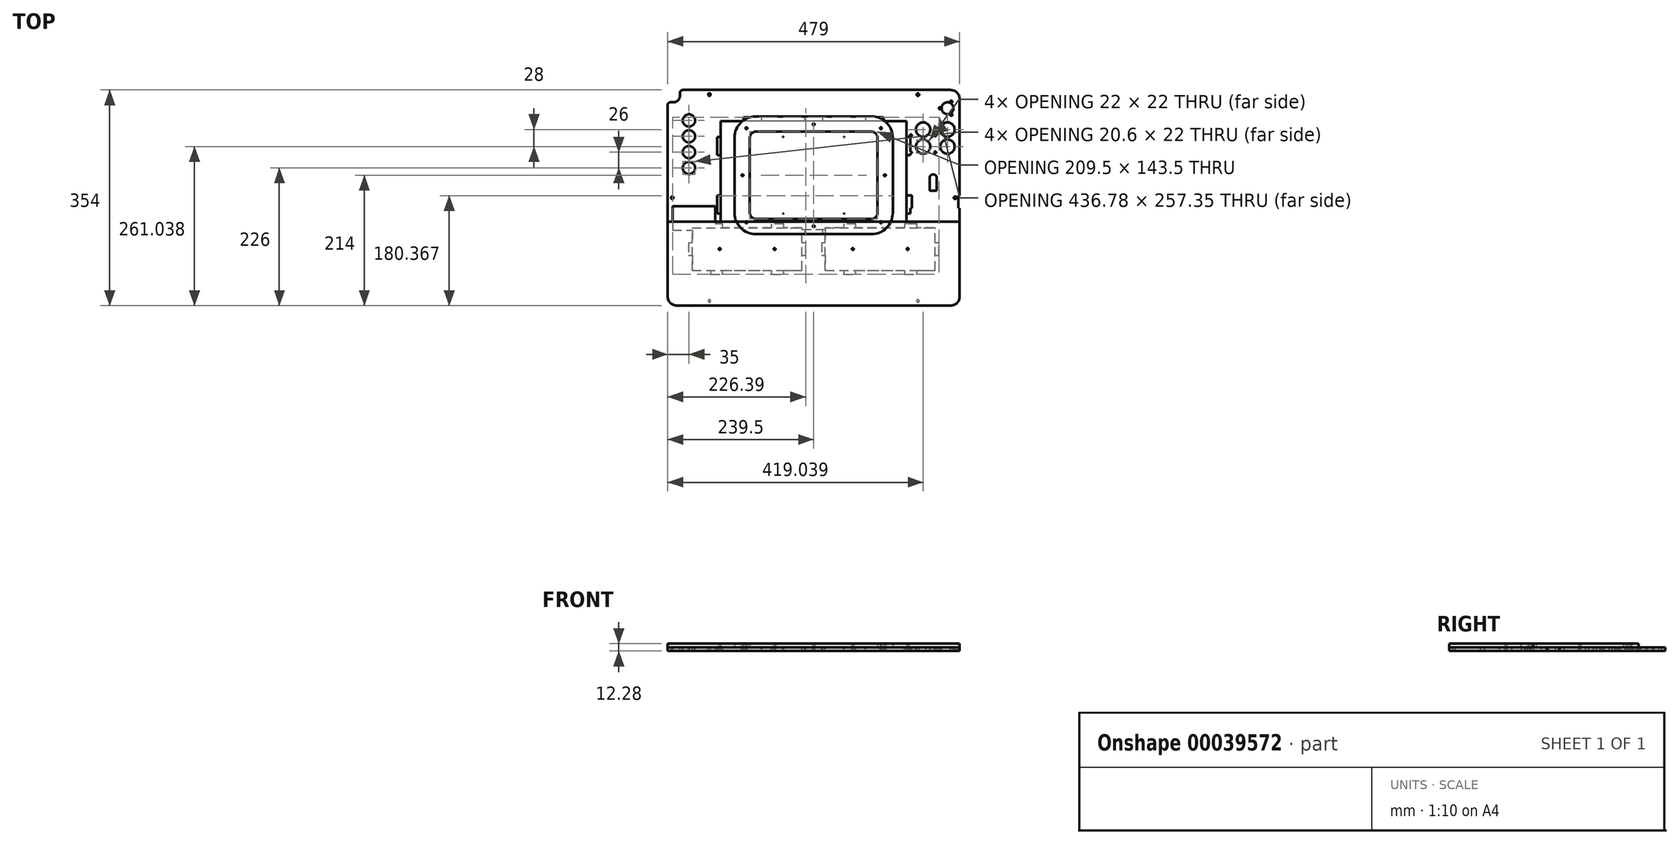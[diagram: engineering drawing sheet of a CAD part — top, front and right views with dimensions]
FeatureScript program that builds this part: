
annotation { "Feature Type Name" : "Feature", "Feature Type Description" : "" }
export const myFeature = defineFeature(function(context is Context, id is Id, definition is map)
    precondition{}
    {
        {
            assignVariable(context, id + "F0", {"name" : "PanelThickness", "anyValue" : 6.14});
        }
        {
            var Q0;
            Q0=qCreatedBy(makeId("Top.planeOp"),FACE);
            var sketch = newSketch(context, id + "F1", { "sketchPlane" : qUnion([Q0])});
            skPoint(sketch, "E0", {"position": v(168.5, 147.5) * mm});
            skPoint(sketch, "E1.visualSharp", {"position": v(237, -199) * mm});
            skPoint(sketch, "E2.visualSharp", {"position": v(-242, -199) * mm});
            skLineSegment(sketch, "E3.rect.right", {"start": v(237, 140) * mm, "end": v(237, -184) * mm});
            skPoint(sketch, "E4", {"position": v(229.5, -22) * mm});
            skPoint(sketch, "E5.visualSharp", {"position": v(-222, 135) * mm});
            skPoint(sketch, "E6.visualSharp", {"position": v(237, 155) * mm});
            skLineSegment(sketch, "E7", {"start": v(-249.24, -22) * mm, "end": v(312.3, -22) * mm, "construction": true});
            skPoint(sketch, "E8", {"position": v(-173.5, 147.5) * mm});
            skPoint(sketch, "E9.visualSharp", {"position": v(-242, 155) * mm});
            skLineSegment(sketch, "E10", {"start": v(0, 155) * mm, "end": v(0, -199) * mm, "construction": true});
            skLineSegment(sketch, "E11.0", {"start": v(-222, 147.5) * mm, "end": v(237, 147.5) * mm, "construction": true});
            skLineSegment(sketch, "E12.0", {"start": v(-242, -191.5) * mm, "end": v(237, -191.5) * mm, "construction": true});
            skLineSegment(sketch, "E13.0", {"start": v(-234.5, 155) * mm, "end": v(-234.5, -199) * mm, "construction": true});
            skLineSegment(sketch, "E3.rect.top", {"start": v(-227, -199) * mm, "end": v(222, -199) * mm});
            skLineSegment(sketch, "E3.rect.left", {"start": v(-242, 130) * mm, "end": v(-242, -184) * mm});
            skPoint(sketch, "E14", {"position": v(-234.5, -22) * mm});
            skLineSegment(sketch, "E3.rect.bottom", {"start": v(-217, 155) * mm, "end": v(222, 155) * mm});
            skLineSegment(sketch, "E15", {"start": v(168.5, -197.31) * mm, "end": v(168.5, 217.61) * mm, "construction": true});
            skLineSegment(sketch, "E16", {"start": v(-173.5, 155) * mm, "end": v(-173.5, -199) * mm, "construction": true});
            skLineSegment(sketch, "E17.0", {"start": v(229.5, 155) * mm, "end": v(229.5, -199) * mm, "construction": true});
            skLineSegment(sketch, "E18.left", {"start": v(-242, 146.2) * mm, "end": v(-242, 155) * mm, "construction": true});
            skLineSegment(sketch, "E18.bottom", {"start": v(-237, 135) * mm, "end": v(-232, 135) * mm});
            skCircle(sketch, "E19", {"center": v(-173.5, -191.5) * mm, "radius": 2.1 * mm});
            skArc(sketch, "E5.filletArc", {"start": v(-232, 135) * mm, "mid": v(-224.93, 137.93) * mm, "end": v(-222, 145) * mm});
            skCircle(sketch, "E20", {"center": v(168.5, 147.5) * mm, "radius": 2.1 * mm});
            skCircle(sketch, "E21", {"center": v(229.5, -22) * mm, "radius": 2.1 * mm});
            skCircle(sketch, "E22", {"center": v(168.5, -191.5) * mm, "radius": 2.1 * mm});
            skCircle(sketch, "E23", {"center": v(-234.5, -22) * mm, "radius": 2.1 * mm});
            skCircle(sketch, "E24", {"center": v(-173.5, 147.5) * mm, "radius": 2.1 * mm});
            skLineSegment(sketch, "E18.right", {"start": v(-222, 145) * mm, "end": v(-222, 150) * mm});
            skArc(sketch, "E25.filletArc", {"start": v(-237, 135) * mm, "mid": v(-240.54, 133.54) * mm, "end": v(-242, 130) * mm});
            skArc(sketch, "E26.filletArc", {"start": v(-217, 155) * mm, "mid": v(-220.54, 153.54) * mm, "end": v(-222, 150) * mm});
            skPoint(sketch, "E27", {"position": v(0, -22) * mm});
            skLineSegment(sketch, "E28", {"start": v(-242, 140) * mm, "end": v(-242, 130) * mm, "construction": true});
            skLineSegment(sketch, "E29", {"start": v(-234.5, 155) * mm, "end": v(-217, 155) * mm, "construction": true});
            skArc(sketch, "E30.filletArc", {"start": v(222, -199) * mm, "mid": v(232.6, -194.6) * mm, "end": v(237, -184) * mm});
            skArc(sketch, "E31.filletArc", {"start": v(-242, -184) * mm, "mid": v(-237.6, -194.6) * mm, "end": v(-227, -199) * mm});
            skArc(sketch, "E32.filletArc", {"start": v(237, 140) * mm, "mid": v(232.6, 150.6) * mm, "end": v(222, 155) * mm});
            skSolve(sketch);
        }
        {
            var Q0;
            Q0=qCreatedBy(makeId("Top.planeOp"),FACE);
            var sketch = newSketch(context, id + "F2", { "sketchPlane" : qUnion([Q0])});
            skLineSegment(sketch, "E33.bottom", {"start": v(-234, -36) * mm, "end": v(-164, -36) * mm});
            skLineSegment(sketch, "E33.top", {"start": v(-234, -75) * mm, "end": v(-164, -75) * mm});
            skLineSegment(sketch, "E33.right", {"start": v(-164, -36) * mm, "end": v(-164, -75) * mm});
            skLineSegment(sketch, "E33.left", {"start": v(-234, -36) * mm, "end": v(-234, -75) * mm});
            skLineSegment(sketch, "E34.0", {"start": v(-242, 130) * mm, "end": v(-242, -184) * mm});
            skLineSegment(sketch, "E35.0", {"start": v(-217, 155) * mm, "end": v(222, 155) * mm});
            skLineSegment(sketch, "E36.1", {"start": v(-238.1, -33.9) * mm, "end": v(-159.9, -33.9) * mm, "construction": true});
            skLineSegment(sketch, "E37.0", {"start": v(-159.9, -33.9) * mm, "end": v(-159.9, -77.1) * mm, "construction": true});
            skLineSegment(sketch, "E38.0", {"start": v(-238.1, -33.9) * mm, "end": v(-238.1, -77.1) * mm, "construction": true});
            skLineSegment(sketch, "E39.0", {"start": v(-238.1, -77.1) * mm, "end": v(-159.9, -77.1) * mm, "construction": true});
            skSolve(sketch);
        }
        {
            var Q0;
            Q0=qCreatedBy(makeId("Top.planeOp"),FACE);
            var sketch = newSketch(context, id + "F3", { "sketchPlane" : qUnion([Q0])});
            skLineSegment(sketch, "E40", {"start": v(-2.5, 81.1) * mm, "end": v(-2.5, -181.33) * mm, "construction": true});
            skLineSegment(sketch, "E41", {"start": v(-21.64, -116.17) * mm, "end": v(-21.64, -141.17) * mm});
            skLineSegment(sketch, "E42", {"start": v(-171.64, -71.17) * mm, "end": v(-201.64, -71.17) * mm});
            skLineSegment(sketch, "E43.0", {"start": v(-15.5, -65.03) * mm, "end": v(-15.5, -147.3) * mm, "construction": true});
            skLineSegment(sketch, "E44", {"start": v(-171.64, -141.17) * mm, "end": v(-201.64, -141.17) * mm});
            skLineSegment(sketch, "E45.MirrorCS", {"start": v(-71.64, -65.03) * mm, "end": v(-51.64, -65.03) * mm});
            skLineSegment(sketch, "E46.rect.bottom", {"start": v(-21.64, -71.17) * mm, "end": v(-51.64, -71.17) * mm});
            skLineSegment(sketch, "E46.rect.top", {"start": v(-21.64, -141.17) * mm, "end": v(-51.64, -141.17) * mm});
            skLineSegment(sketch, "E46.rect.left", {"start": v(-21.64, -71.17) * mm, "end": v(-21.64, -96.17) * mm});
            skLineSegment(sketch, "E46.rect.right", {"start": v(-201.64, -71.17) * mm, "end": v(-201.64, -96.17) * mm});
            skPoint(sketch, "E47", {"position": v(-207.78, -106.17) * mm});
            skLineSegment(sketch, "E48.top", {"start": v(-71.64, -147.3) * mm, "end": v(-51.64, -147.3) * mm});
            skLineSegment(sketch, "E49.MirrorCS", {"start": v(-151.64, -147.3) * mm, "end": v(-171.64, -147.3) * mm});
            skLineSegment(sketch, "E50", {"start": v(-71.64, -71.17) * mm, "end": v(-151.64, -71.17) * mm});
            skLineSegment(sketch, "E51.0", {"start": v(-15.5, -147.3) * mm, "end": v(-207.78, -147.3) * mm, "construction": true});
            skLineSegment(sketch, "E52.0", {"start": v(-207.78, -65.03) * mm, "end": v(-207.78, -147.3) * mm, "construction": true});
            skLineSegment(sketch, "E53.0", {"start": v(-15.5, -65.03) * mm, "end": v(-207.78, -65.03) * mm, "construction": true});
            skLineSegment(sketch, "E54", {"start": v(-201.64, -116.17) * mm, "end": v(-201.64, -141.17) * mm});
            skLineSegment(sketch, "E55.MirrorCS", {"start": v(-15.5, -116.17) * mm, "end": v(-15.5, -96.17) * mm});
            skLineSegment(sketch, "E56", {"start": v(-71.64, -141.17) * mm, "end": v(-151.64, -141.17) * mm});
            skLineSegment(sketch, "E57.right", {"start": v(-207.78, -116.17) * mm, "end": v(-207.78, -96.17) * mm});
            skLineSegment(sketch, "E58.MirrorCS", {"start": v(-21.64, -96.17) * mm, "end": v(-15.5, -96.17) * mm});
            skLineSegment(sketch, "E59.MirrorCS", {"start": v(-21.64, -116.17) * mm, "end": v(-15.5, -116.17) * mm});
            skLineSegment(sketch, "E57.top", {"start": v(-201.64, -96.17) * mm, "end": v(-207.78, -96.17) * mm});
            skLineSegment(sketch, "E60.MirrorCS", {"start": v(-71.64, -71.17) * mm, "end": v(-71.64, -65.03) * mm});
            skLineSegment(sketch, "E61.MirrorCS", {"start": v(-51.64, -71.17) * mm, "end": v(-51.64, -65.03) * mm});
            skLineSegment(sketch, "E48.left", {"start": v(-71.64, -141.17) * mm, "end": v(-71.64, -147.3) * mm});
            skLineSegment(sketch, "E48.right", {"start": v(-51.64, -141.17) * mm, "end": v(-51.64, -147.3) * mm});
            skLineSegment(sketch, "E62.MirrorCS", {"start": v(-151.64, -141.17) * mm, "end": v(-151.64, -147.3) * mm});
            skLineSegment(sketch, "E63.MirrorCS", {"start": v(-171.64, -141.17) * mm, "end": v(-171.64, -147.3) * mm});
            skLineSegment(sketch, "E57.bottom", {"start": v(-201.64, -116.17) * mm, "end": v(-207.78, -116.17) * mm});
            skLineSegment(sketch, "E64.MirrorCS", {"start": v(16.64, -96.17) * mm, "end": v(10.5, -96.17) * mm});
            skLineSegment(sketch, "E65.MirrorCS", {"start": v(16.64, -116.17) * mm, "end": v(10.5, -116.17) * mm});
            skPoint(sketch, "E66.MirrorP", {"position": v(202.78, -106.17) * mm});
            skLineSegment(sketch, "E67.MirrorCS", {"start": v(146.64, -71.17) * mm, "end": v(146.64, -65.03) * mm});
            skLineSegment(sketch, "E68.MirrorCS", {"start": v(202.78, -65.03) * mm, "end": v(202.78, -147.3) * mm, "construction": true});
            skLineSegment(sketch, "E69.MirrorCS", {"start": v(166.64, -71.17) * mm, "end": v(166.64, -65.03) * mm});
            skLineSegment(sketch, "E70.MirrorCS", {"start": v(10.5, -65.03) * mm, "end": v(202.78, -65.03) * mm, "construction": true});
            skLineSegment(sketch, "E71.MirrorCS", {"start": v(196.64, -116.17) * mm, "end": v(202.78, -116.17) * mm});
            skLineSegment(sketch, "E72.MirrorCS", {"start": v(16.64, -116.17) * mm, "end": v(16.64, -141.17) * mm});
            skLineSegment(sketch, "E73.MirrorCS", {"start": v(196.64, -116.17) * mm, "end": v(196.64, -141.17) * mm});
            skLineSegment(sketch, "E74.MirrorCS", {"start": v(10.5, -116.17) * mm, "end": v(10.5, -96.17) * mm});
            skLineSegment(sketch, "E75.MirrorCS", {"start": v(166.64, -71.17) * mm, "end": v(196.64, -71.17) * mm});
            skLineSegment(sketch, "E76.MirrorCS", {"start": v(66.64, -141.17) * mm, "end": v(146.64, -141.17) * mm});
            skLineSegment(sketch, "E77.MirrorCS", {"start": v(10.5, -65.03) * mm, "end": v(10.5, -147.3) * mm, "construction": true});
            skLineSegment(sketch, "E78.MirrorCS", {"start": v(202.78, -116.17) * mm, "end": v(202.78, -96.17) * mm});
            skLineSegment(sketch, "E79.MirrorCS", {"start": v(166.64, -141.17) * mm, "end": v(196.64, -141.17) * mm});
            skLineSegment(sketch, "E80.MirrorCS", {"start": v(10.5, -147.3) * mm, "end": v(202.78, -147.3) * mm, "construction": true});
            skLineSegment(sketch, "E81.MirrorCS", {"start": v(66.64, -65.03) * mm, "end": v(46.64, -65.03) * mm});
            skLineSegment(sketch, "E82.MirrorCS", {"start": v(16.64, -71.17) * mm, "end": v(46.64, -71.17) * mm});
            skLineSegment(sketch, "E83.MirrorCS", {"start": v(66.64, -71.17) * mm, "end": v(66.64, -65.03) * mm});
            skLineSegment(sketch, "E84.MirrorCS", {"start": v(16.64, -71.17) * mm, "end": v(16.64, -96.17) * mm});
            skLineSegment(sketch, "E85.MirrorCS", {"start": v(46.64, -71.17) * mm, "end": v(46.64, -65.03) * mm});
            skLineSegment(sketch, "E86.MirrorCS", {"start": v(196.64, -71.17) * mm, "end": v(196.64, -96.17) * mm});
            skLineSegment(sketch, "E87.MirrorCS", {"start": v(66.64, -141.17) * mm, "end": v(66.64, -147.3) * mm});
            skLineSegment(sketch, "E88.MirrorCS", {"start": v(66.64, -147.3) * mm, "end": v(46.64, -147.3) * mm});
            skLineSegment(sketch, "E89.MirrorCS", {"start": v(46.64, -141.17) * mm, "end": v(46.64, -147.3) * mm});
            skLineSegment(sketch, "E90.MirrorCS", {"start": v(146.64, -147.3) * mm, "end": v(166.64, -147.3) * mm});
            skLineSegment(sketch, "E91.MirrorCS", {"start": v(146.64, -141.17) * mm, "end": v(146.64, -147.3) * mm});
            skLineSegment(sketch, "E92.MirrorCS", {"start": v(146.64, -65.03) * mm, "end": v(166.64, -65.03) * mm});
            skLineSegment(sketch, "E93.MirrorCS", {"start": v(16.64, -141.17) * mm, "end": v(46.64, -141.17) * mm});
            skLineSegment(sketch, "E94.MirrorCS", {"start": v(196.64, -96.17) * mm, "end": v(202.78, -96.17) * mm});
            skLineSegment(sketch, "E95.MirrorCS", {"start": v(66.64, -71.17) * mm, "end": v(146.64, -71.17) * mm});
            skLineSegment(sketch, "E96.MirrorCS", {"start": v(166.64, -141.17) * mm, "end": v(166.64, -147.3) * mm});
            skPoint(sketch, "E97", {"position": v(-2.5, 7.7) * mm});
            skLineSegment(sketch, "E98", {"start": v(-207.78, -106.17) * mm, "end": v(-15.5, -106.17) * mm, "construction": true});
            skLineSegment(sketch, "E99.MirrorCS", {"start": v(-171.64, -71.17) * mm, "end": v(-171.64, -65.03) * mm});
            skLineSegment(sketch, "E100.MirrorCS", {"start": v(-151.64, -65.03) * mm, "end": v(-171.64, -65.03) * mm});
            skLineSegment(sketch, "E101.MirrorCS", {"start": v(-151.64, -71.17) * mm, "end": v(-151.64, -65.03) * mm});
            skPoint(sketch, "E102", {"position": v(-111.64, -106.17) * mm});
            skLineSegment(sketch, "E103", {"start": v(-111.64, -71.17) * mm, "end": v(-111.64, -141.17) * mm, "construction": true});
            skPoint(sketch, "E104", {"position": v(-2.5, 7.83) * mm});
            skLineSegment(sketch, "E105", {"start": v(-2.5, 7.7) * mm, "end": v(229.5, -22) * mm, "construction": true});
            skLineSegment(sketch, "E106", {"start": v(-234.5, -22) * mm, "end": v(-2.5, 7.7) * mm, "construction": true});
            skCircle(sketch, "E107.0", {"center": v(-234.5, -22) * mm, "radius": 2.1 * mm});
            skCircle(sketch, "E107.1", {"center": v(229.5, -22) * mm, "radius": 2.1 * mm});
            skSolve(sketch);
        }
        {
            var Q0;
            Q0=qCreatedBy(makeId("Top.planeOp"),FACE);
            var sketch = newSketch(context, id + "F4", { "sketchPlane" : qUnion([Q0])});
            skLineSegment(sketch, "E108.0", {"start": v(-242, 130) * mm, "end": v(-242, -184) * mm});
            skLineSegment(sketch, "E108.1", {"start": v(-217, 155) * mm, "end": v(222, 155) * mm});
            skPoint(sketch, "E109", {"position": v(-207, 107.8) * mm});
            skPoint(sketch, "E110", {"position": v(-205.95, 105) * mm});
            skPoint(sketch, "E111", {"position": v(-207, 102.2) * mm});
            skArc(sketch, "E112", {"start": v(-205.95, 95.06) * mm, "mid": v(-200.59, 97.33) * mm, "end": v(-197.4, 102.2) * mm});
            skArc(sketch, "E113", {"start": v(-216.6, 102.2) * mm, "mid": v(-213.41, 97.33) * mm, "end": v(-208.05, 95.06) * mm});
            skArc(sketch, "E114", {"start": v(-197.4, 107.8) * mm, "mid": v(-200.59, 112.67) * mm, "end": v(-205.95, 114.94) * mm});
            skPoint(sketch, "E115", {"position": v(-208.05, 105) * mm});
            skArc(sketch, "E116", {"start": v(-208.05, 114.94) * mm, "mid": v(-213.41, 112.67) * mm, "end": v(-216.6, 107.8) * mm});
            skCircle(sketch, "E117", {"center": v(-207, 105) * mm, "radius": 11.5 * mm, "construction": true});
            skLineSegment(sketch, "E118", {"start": v(-197.4, 107.8) * mm, "end": v(-216.6, 107.8) * mm, "construction": true});
            skLineSegment(sketch, "E119", {"start": v(-205.95, 114.94) * mm, "end": v(-205.95, 95.06) * mm, "construction": true});
            skLineSegment(sketch, "E120", {"start": v(-197.4, 102.2) * mm, "end": v(-216.6, 102.2) * mm, "construction": true});
            skLineSegment(sketch, "E121", {"start": v(-208.05, 114.94) * mm, "end": v(-208.05, 95.06) * mm, "construction": true});
            skLineSegment(sketch, "E122", {"start": v(-196.7, 105) * mm, "end": v(-217.3, 105) * mm, "construction": true});
            skLineSegment(sketch, "E123", {"start": v(-207, 116) * mm, "end": v(-207, 94) * mm, "construction": true});
            skLineSegment(sketch, "E124", {"start": v(-197.4, 107.8) * mm, "end": v(-196.7, 107.8) * mm});
            skLineSegment(sketch, "E125", {"start": v(-216.6, 107.8) * mm, "end": v(-217.3, 107.8) * mm});
            skLineSegment(sketch, "E126", {"start": v(-208.05, 95.06) * mm, "end": v(-208.05, 94) * mm});
            skLineSegment(sketch, "E127", {"start": v(-205.95, 94) * mm, "end": v(-208.05, 94) * mm});
            skLineSegment(sketch, "E128.rect.right", {"start": v(-217.3, 102.2) * mm, "end": v(-217.3, 107.8) * mm});
            skLineSegment(sketch, "E128.rect.left", {"start": v(-196.7, 102.2) * mm, "end": v(-196.7, 107.8) * mm});
            skLineSegment(sketch, "E128.rect.bottom", {"start": v(-196.7, 102.2) * mm, "end": v(-197.4, 102.2) * mm});
            skLineSegment(sketch, "E129", {"start": v(-216.6, 102.2) * mm, "end": v(-217.3, 102.2) * mm});
            skLineSegment(sketch, "E130", {"start": v(-205.95, 95.06) * mm, "end": v(-205.95, 94) * mm});
            skLineSegment(sketch, "E131.MirrorCS", {"start": v(-208.05, 114.94) * mm, "end": v(-208.05, 116) * mm});
            skLineSegment(sketch, "E132.MirrorCS", {"start": v(-205.95, 114.94) * mm, "end": v(-205.95, 116) * mm});
            skLineSegment(sketch, "E133.MirrorCS", {"start": v(-205.95, 116) * mm, "end": v(-208.05, 116) * mm});
            skCircle(sketch, "E134.0.1.0", {"center": v(-207, 79) * mm, "radius": 11.5 * mm, "construction": true});
            skPoint(sketch, "E134.0.1.1", {"position": v(-208.05, 79) * mm});
            skLineSegment(sketch, "E134.0.1.2", {"start": v(-207, 90) * mm, "end": v(-207, 68) * mm, "construction": true});
            skArc(sketch, "E134.0.1.3", {"start": v(-205.95, 69.06) * mm, "mid": v(-200.59, 71.33) * mm, "end": v(-197.4, 76.2) * mm});
            skLineSegment(sketch, "E134.0.1.4", {"start": v(-217.3, 76.2) * mm, "end": v(-217.3, 81.8) * mm});
            skLineSegment(sketch, "E134.0.1.5", {"start": v(-205.95, 88.94) * mm, "end": v(-205.95, 69.06) * mm, "construction": true});
            skArc(sketch, "E134.0.1.6", {"start": v(-208.05, 88.94) * mm, "mid": v(-213.41, 86.67) * mm, "end": v(-216.6, 81.8) * mm});
            skLineSegment(sketch, "E134.0.1.7", {"start": v(-196.7, 79) * mm, "end": v(-217.3, 79) * mm, "construction": true});
            skLineSegment(sketch, "E134.0.1.8", {"start": v(-208.05, 88.94) * mm, "end": v(-208.05, 69.06) * mm, "construction": true});
            skPoint(sketch, "E134.0.1.9", {"position": v(-207, 76.2) * mm});
            skPoint(sketch, "E134.0.1.10", {"position": v(-207, 79) * mm});
            skArc(sketch, "E134.0.1.11", {"start": v(-197.4, 81.8) * mm, "mid": v(-200.59, 86.67) * mm, "end": v(-205.95, 88.94) * mm});
            skPoint(sketch, "E134.0.1.12", {"position": v(-205.95, 79) * mm});
            skLineSegment(sketch, "E134.0.1.13", {"start": v(-197.4, 81.8) * mm, "end": v(-216.6, 81.8) * mm, "construction": true});
            skPoint(sketch, "E134.0.1.14", {"position": v(-207, 81.8) * mm});
            skLineSegment(sketch, "E134.0.1.15", {"start": v(-196.7, 76.2) * mm, "end": v(-196.7, 81.8) * mm});
            skLineSegment(sketch, "E134.0.1.16", {"start": v(-197.4, 76.2) * mm, "end": v(-216.6, 76.2) * mm, "construction": true});
            skArc(sketch, "E134.0.1.17", {"start": v(-216.6, 76.2) * mm, "mid": v(-213.41, 71.33) * mm, "end": v(-208.05, 69.06) * mm});
            skPoint(sketch, "E134.0.1.18", {"position": v(-207, 79) * mm});
            skLineSegment(sketch, "E134.0.1.19", {"start": v(-205.95, 68) * mm, "end": v(-208.05, 68) * mm});
            skLineSegment(sketch, "E134.0.1.20", {"start": v(-197.4, 81.8) * mm, "end": v(-196.7, 81.8) * mm});
            skLineSegment(sketch, "E134.0.1.21", {"start": v(-205.95, 90) * mm, "end": v(-208.05, 90) * mm});
            skLineSegment(sketch, "E134.0.1.22", {"start": v(-208.05, 88.94) * mm, "end": v(-208.05, 90) * mm});
            skLineSegment(sketch, "E134.0.1.23", {"start": v(-208.05, 69.06) * mm, "end": v(-208.05, 68) * mm});
            skLineSegment(sketch, "E134.0.1.24", {"start": v(-196.7, 76.2) * mm, "end": v(-197.4, 76.2) * mm});
            skLineSegment(sketch, "E134.0.1.25", {"start": v(-205.95, 69.06) * mm, "end": v(-205.95, 68) * mm});
            skLineSegment(sketch, "E134.0.1.26", {"start": v(-216.6, 76.2) * mm, "end": v(-217.3, 76.2) * mm});
            skLineSegment(sketch, "E134.0.1.27", {"start": v(-205.95, 88.94) * mm, "end": v(-205.95, 90) * mm});
            skLineSegment(sketch, "E134.0.1.28", {"start": v(-216.6, 81.8) * mm, "end": v(-217.3, 81.8) * mm});
            skCircle(sketch, "E134.0.2.0", {"center": v(-207, 53) * mm, "radius": 11.5 * mm, "construction": true});
            skPoint(sketch, "E134.0.2.1", {"position": v(-208.05, 53) * mm});
            skLineSegment(sketch, "E134.0.2.2", {"start": v(-207, 64) * mm, "end": v(-207, 42) * mm, "construction": true});
            skArc(sketch, "E134.0.2.3", {"start": v(-205.95, 43.06) * mm, "mid": v(-200.59, 45.33) * mm, "end": v(-197.4, 50.2) * mm});
            skLineSegment(sketch, "E134.0.2.4", {"start": v(-217.3, 50.2) * mm, "end": v(-217.3, 55.8) * mm});
            skLineSegment(sketch, "E134.0.2.5", {"start": v(-205.95, 62.94) * mm, "end": v(-205.95, 43.06) * mm, "construction": true});
            skArc(sketch, "E134.0.2.6", {"start": v(-208.05, 62.94) * mm, "mid": v(-213.41, 60.67) * mm, "end": v(-216.6, 55.8) * mm});
            skLineSegment(sketch, "E134.0.2.7", {"start": v(-196.7, 53) * mm, "end": v(-217.3, 53) * mm, "construction": true});
            skLineSegment(sketch, "E134.0.2.8", {"start": v(-208.05, 62.94) * mm, "end": v(-208.05, 43.06) * mm, "construction": true});
            skPoint(sketch, "E134.0.2.9", {"position": v(-207, 50.2) * mm});
            skPoint(sketch, "E134.0.2.10", {"position": v(-207, 53) * mm});
            skArc(sketch, "E134.0.2.11", {"start": v(-197.4, 55.8) * mm, "mid": v(-200.59, 60.67) * mm, "end": v(-205.95, 62.94) * mm});
            skPoint(sketch, "E134.0.2.12", {"position": v(-205.95, 53) * mm});
            skLineSegment(sketch, "E134.0.2.13", {"start": v(-197.4, 55.8) * mm, "end": v(-216.6, 55.8) * mm, "construction": true});
            skPoint(sketch, "E134.0.2.14", {"position": v(-207, 55.8) * mm});
            skLineSegment(sketch, "E134.0.2.15", {"start": v(-196.7, 50.2) * mm, "end": v(-196.7, 55.8) * mm});
            skLineSegment(sketch, "E134.0.2.16", {"start": v(-197.4, 50.2) * mm, "end": v(-216.6, 50.2) * mm, "construction": true});
            skArc(sketch, "E134.0.2.17", {"start": v(-216.6, 50.2) * mm, "mid": v(-213.41, 45.33) * mm, "end": v(-208.05, 43.06) * mm});
            skPoint(sketch, "E134.0.2.18", {"position": v(-207, 53) * mm});
            skLineSegment(sketch, "E134.0.2.19", {"start": v(-205.95, 42) * mm, "end": v(-208.05, 42) * mm});
            skLineSegment(sketch, "E134.0.2.20", {"start": v(-197.4, 55.8) * mm, "end": v(-196.7, 55.8) * mm});
            skLineSegment(sketch, "E134.0.2.21", {"start": v(-205.95, 64) * mm, "end": v(-208.05, 64) * mm});
            skLineSegment(sketch, "E134.0.2.22", {"start": v(-208.05, 62.94) * mm, "end": v(-208.05, 64) * mm});
            skLineSegment(sketch, "E134.0.2.23", {"start": v(-208.05, 43.06) * mm, "end": v(-208.05, 42) * mm});
            skLineSegment(sketch, "E134.0.2.24", {"start": v(-196.7, 50.2) * mm, "end": v(-197.4, 50.2) * mm});
            skLineSegment(sketch, "E134.0.2.25", {"start": v(-205.95, 43.06) * mm, "end": v(-205.95, 42) * mm});
            skLineSegment(sketch, "E134.0.2.26", {"start": v(-216.6, 50.2) * mm, "end": v(-217.3, 50.2) * mm});
            skLineSegment(sketch, "E134.0.2.27", {"start": v(-205.95, 62.94) * mm, "end": v(-205.95, 64) * mm});
            skLineSegment(sketch, "E134.0.2.28", {"start": v(-216.6, 55.8) * mm, "end": v(-217.3, 55.8) * mm});
            skCircle(sketch, "E134.0.3.0", {"center": v(-207, 27) * mm, "radius": 11.5 * mm, "construction": true});
            skPoint(sketch, "E134.0.3.1", {"position": v(-208.05, 27) * mm});
            skLineSegment(sketch, "E134.0.3.2", {"start": v(-207, 38) * mm, "end": v(-207, 16) * mm, "construction": true});
            skArc(sketch, "E134.0.3.3", {"start": v(-205.95, 17.06) * mm, "mid": v(-200.59, 19.33) * mm, "end": v(-197.4, 24.2) * mm});
            skLineSegment(sketch, "E134.0.3.4", {"start": v(-217.3, 24.2) * mm, "end": v(-217.3, 29.8) * mm});
            skLineSegment(sketch, "E134.0.3.5", {"start": v(-205.95, 36.94) * mm, "end": v(-205.95, 17.06) * mm, "construction": true});
            skArc(sketch, "E134.0.3.6", {"start": v(-208.05, 36.94) * mm, "mid": v(-213.41, 34.67) * mm, "end": v(-216.6, 29.8) * mm});
            skLineSegment(sketch, "E134.0.3.7", {"start": v(-196.7, 27) * mm, "end": v(-217.3, 27) * mm, "construction": true});
            skLineSegment(sketch, "E134.0.3.8", {"start": v(-208.05, 36.94) * mm, "end": v(-208.05, 17.06) * mm, "construction": true});
            skPoint(sketch, "E134.0.3.9", {"position": v(-207, 24.2) * mm});
            skPoint(sketch, "E134.0.3.10", {"position": v(-207, 27) * mm});
            skArc(sketch, "E134.0.3.11", {"start": v(-197.4, 29.8) * mm, "mid": v(-200.59, 34.67) * mm, "end": v(-205.95, 36.94) * mm});
            skPoint(sketch, "E134.0.3.12", {"position": v(-205.95, 27) * mm});
            skLineSegment(sketch, "E134.0.3.13", {"start": v(-197.4, 29.8) * mm, "end": v(-216.6, 29.8) * mm, "construction": true});
            skPoint(sketch, "E134.0.3.14", {"position": v(-207, 29.8) * mm});
            skLineSegment(sketch, "E134.0.3.15", {"start": v(-196.7, 24.2) * mm, "end": v(-196.7, 29.8) * mm});
            skLineSegment(sketch, "E134.0.3.16", {"start": v(-197.4, 24.2) * mm, "end": v(-216.6, 24.2) * mm, "construction": true});
            skArc(sketch, "E134.0.3.17", {"start": v(-216.6, 24.2) * mm, "mid": v(-213.41, 19.33) * mm, "end": v(-208.05, 17.06) * mm});
            skPoint(sketch, "E134.0.3.18", {"position": v(-207, 27) * mm});
            skLineSegment(sketch, "E134.0.3.19", {"start": v(-205.95, 16) * mm, "end": v(-208.05, 16) * mm});
            skLineSegment(sketch, "E134.0.3.20", {"start": v(-197.4, 29.8) * mm, "end": v(-196.7, 29.8) * mm});
            skLineSegment(sketch, "E134.0.3.21", {"start": v(-205.95, 38) * mm, "end": v(-208.05, 38) * mm});
            skLineSegment(sketch, "E134.0.3.22", {"start": v(-208.05, 36.94) * mm, "end": v(-208.05, 38) * mm});
            skLineSegment(sketch, "E134.0.3.23", {"start": v(-208.05, 17.06) * mm, "end": v(-208.05, 16) * mm});
            skLineSegment(sketch, "E134.0.3.24", {"start": v(-196.7, 24.2) * mm, "end": v(-197.4, 24.2) * mm});
            skLineSegment(sketch, "E134.0.3.25", {"start": v(-205.95, 17.06) * mm, "end": v(-205.95, 16) * mm});
            skLineSegment(sketch, "E134.0.3.26", {"start": v(-216.6, 24.2) * mm, "end": v(-217.3, 24.2) * mm});
            skLineSegment(sketch, "E134.0.3.27", {"start": v(-205.95, 36.94) * mm, "end": v(-205.95, 38) * mm});
            skLineSegment(sketch, "E134.0.3.28", {"start": v(-216.6, 29.8) * mm, "end": v(-217.3, 29.8) * mm});
            skLineSegment(sketch, "E134.direction1", {"start": v(-207, 105) * mm, "end": v(-181.18, 105) * mm, "construction": true});
            skLineSegment(sketch, "E134.direction2", {"start": v(-207, 105) * mm, "end": v(-207, 79) * mm, "construction": true});
            skSolve(sketch);
        }
        {
            var Q0;
            Q0=qCreatedBy(makeId("Top.planeOp"),FACE);
            var sketch = newSketch(context, id + "F5", { "sketchPlane" : qUnion([Q0])});
            skLineSegment(sketch, "E135.MirrorCS", {"start": v(217, 77) * mm, "end": v(232.5, 77) * mm, "construction": true});
            skLineSegment(sketch, "E136.right", {"start": v(201.5, 90) * mm, "end": v(201.5, 103) * mm, "construction": true});
            skLineSegment(sketch, "E137.MirrorCS", {"start": v(232.5, 90) * mm, "end": v(232.5, 103) * mm, "construction": true});
            skLineSegment(sketch, "E138.MirrorCS", {"start": v(217, 103) * mm, "end": v(232.5, 103) * mm, "construction": true});
            skLineSegment(sketch, "E139", {"start": v(196.44, 90) * mm, "end": v(221.62, 90) * mm, "construction": true});
            skCircle(sketch, "E140.MirrorC", {"center": v(217, 90) * mm, "radius": 11.8 * mm});
            skLineSegment(sketch, "E141", {"start": v(217, 78.2) * mm, "end": v(217, 132.46) * mm, "construction": true});
            skLineSegment(sketch, "E142.MirrorCS", {"start": v(232.5, 90) * mm, "end": v(232.5, 77) * mm, "construction": true});
            skLineSegment(sketch, "E136.bottom", {"start": v(217, 90) * mm, "end": v(196.97, 90) * mm, "construction": true});
            skLineSegment(sketch, "E136.top", {"start": v(217, 103) * mm, "end": v(201.5, 103) * mm, "construction": true});
            skLineSegment(sketch, "E143.MirrorCS", {"start": v(217, 77) * mm, "end": v(201.5, 77) * mm, "construction": true});
            skLineSegment(sketch, "E136.left", {"start": v(217, 90) * mm, "end": v(217, 103) * mm, "construction": true});
            skLineSegment(sketch, "E144.MirrorCS", {"start": v(201.5, 90) * mm, "end": v(201.5, 77) * mm, "construction": true});
            skLineSegment(sketch, "E145.MirrorCS", {"start": v(220.99, 102.86) * mm, "end": v(220.99, 96.38) * mm, "construction": true});
            skLineSegment(sketch, "E146.MirrorCS", {"start": v(224.8, 99.5) * mm, "end": v(219, 99.5) * mm, "construction": true});
            skLineSegment(sketch, "E147.MirrorCS", {"start": v(196.99, 83.86) * mm, "end": v(196.99, 76.51) * mm, "construction": true});
            skCircle(sketch, "E148.MirrorC", {"center": v(220.99, 99.5) * mm, "radius": 1.55 * mm});
            skLineSegment(sketch, "E149.MirrorCS", {"start": v(198.8, 80.5) * mm, "end": v(195, 80.5) * mm, "construction": true});
            skCircle(sketch, "E150.MirrorC", {"center": v(196.99, 80.5) * mm, "radius": 1.55 * mm});
            skLineSegment(sketch, "E151.0", {"start": v(237, 140) * mm, "end": v(237, -184) * mm});
            skLineSegment(sketch, "E151.1", {"start": v(-217, 155) * mm, "end": v(222, 155) * mm});
            skLineSegment(sketch, "E152.0.1.0", {"start": v(217, 49) * mm, "end": v(201.5, 49) * mm, "construction": true});
            skLineSegment(sketch, "E152.0.1.1", {"start": v(217, 62) * mm, "end": v(217, 75) * mm, "construction": true});
            skLineSegment(sketch, "E152.0.1.2", {"start": v(196.44, 62) * mm, "end": v(221.62, 62) * mm, "construction": true});
            skCircle(sketch, "E152.0.1.3", {"center": v(217, 62) * mm, "radius": 11.8 * mm});
            skLineSegment(sketch, "E152.0.1.4", {"start": v(217, 50.2) * mm, "end": v(217, 104.46) * mm, "construction": true});
            skLineSegment(sketch, "E152.0.1.5", {"start": v(232.5, 62) * mm, "end": v(232.5, 49) * mm, "construction": true});
            skLineSegment(sketch, "E152.0.1.6", {"start": v(217, 62) * mm, "end": v(196.97, 62) * mm, "construction": true});
            skLineSegment(sketch, "E152.0.1.7", {"start": v(217, 75) * mm, "end": v(201.5, 75) * mm, "construction": true});
            skLineSegment(sketch, "E152.0.1.8", {"start": v(217, 75) * mm, "end": v(232.5, 75) * mm, "construction": true});
            skLineSegment(sketch, "E152.0.1.9", {"start": v(232.5, 62) * mm, "end": v(232.5, 75) * mm, "construction": true});
            skLineSegment(sketch, "E152.0.1.10", {"start": v(201.5, 62) * mm, "end": v(201.5, 75) * mm, "construction": true});
            skLineSegment(sketch, "E152.0.1.11", {"start": v(217, 49) * mm, "end": v(232.5, 49) * mm, "construction": true});
            skLineSegment(sketch, "E152.0.1.12", {"start": v(201.5, 62) * mm, "end": v(201.5, 49) * mm, "construction": true});
            skLineSegment(sketch, "E152.0.1.13", {"start": v(224.8, 71.5) * mm, "end": v(219, 71.5) * mm, "construction": true});
            skLineSegment(sketch, "E152.0.1.14", {"start": v(220.99, 74.86) * mm, "end": v(220.99, 68.38) * mm, "construction": true});
            skCircle(sketch, "E152.0.1.15", {"center": v(220.99, 71.5) * mm, "radius": 1.55 * mm});
            skCircle(sketch, "E152.0.1.16", {"center": v(217, 62) * mm, "radius": 11.8 * mm});
            skLineSegment(sketch, "E152.0.1.17", {"start": v(196.99, 55.86) * mm, "end": v(196.99, 48.51) * mm, "construction": true});
            skLineSegment(sketch, "E152.0.1.18", {"start": v(198.8, 52.5) * mm, "end": v(195, 52.5) * mm, "construction": true});
            skCircle(sketch, "E152.0.1.19", {"center": v(196.99, 52.5) * mm, "radius": 1.55 * mm});
            skLineSegment(sketch, "E152.direction1", {"start": v(201.5, 77) * mm, "end": v(219, 77) * mm, "construction": true});
            skLineSegment(sketch, "E152.direction2", {"start": v(201.5, 77) * mm, "end": v(201.5, 49) * mm, "construction": true});
            skCircle(sketch, "E153", {"center": v(217, 125) * mm, "radius": 12.5 * mm, "construction": true});
            skCircle(sketch, "E154", {"center": v(217, 125) * mm, "radius": 16 * mm, "construction": true});
            skCircle(sketch, "E155", {"center": v(204.5, 125) * mm, "radius": 1.75 * mm});
            skCircle(sketch, "E156.1.0", {"center": v(223.25, 114.17) * mm, "radius": 1.75 * mm});
            skCircle(sketch, "E156.2.0", {"center": v(223.25, 135.83) * mm, "radius": 1.75 * mm});
            skCircle(sketch, "E157", {"center": v(217, 125) * mm, "radius": 9.75 * mm});
            skLineSegment(sketch, "E158.0.1.0", {"start": v(177, 77) * mm, "end": v(161.5, 77) * mm, "construction": true});
            skLineSegment(sketch, "E158.3.1.0", {"start": v(177, 90) * mm, "end": v(177, 103) * mm, "construction": true});
            skLineSegment(sketch, "E158.6.1.0", {"start": v(156.44, 90) * mm, "end": v(181.62, 90) * mm, "construction": true});
            skCircle(sketch, "E158.9.1.0", {"center": v(177, 90) * mm, "radius": 11.8 * mm});
            skLineSegment(sketch, "E158.11.1.0", {"start": v(177, 78.2) * mm, "end": v(177, 132.46) * mm, "construction": true});
            skLineSegment(sketch, "E158.14.1.0", {"start": v(192.5, 90) * mm, "end": v(192.5, 77) * mm, "construction": true});
            skLineSegment(sketch, "E158.17.1.0", {"start": v(177, 90) * mm, "end": v(156.97, 90) * mm, "construction": true});
            skLineSegment(sketch, "E158.20.1.0", {"start": v(177, 103) * mm, "end": v(161.5, 103) * mm, "construction": true});
            skLineSegment(sketch, "E158.23.1.0", {"start": v(177, 103) * mm, "end": v(192.5, 103) * mm, "construction": true});
            skLineSegment(sketch, "E158.26.1.0", {"start": v(192.5, 90) * mm, "end": v(192.5, 103) * mm, "construction": true});
            skLineSegment(sketch, "E158.29.1.0", {"start": v(161.5, 90) * mm, "end": v(161.5, 103) * mm, "construction": true});
            skLineSegment(sketch, "E158.32.1.0", {"start": v(177, 77) * mm, "end": v(192.5, 77) * mm, "construction": true});
            skLineSegment(sketch, "E158.35.1.0", {"start": v(161.5, 90) * mm, "end": v(161.5, 77) * mm, "construction": true});
            skLineSegment(sketch, "E158.38.1.0", {"start": v(184.8, 99.5) * mm, "end": v(179, 99.5) * mm, "construction": true});
            skLineSegment(sketch, "E158.41.1.0", {"start": v(180.99, 102.86) * mm, "end": v(180.99, 96.38) * mm, "construction": true});
            skCircle(sketch, "E158.44.1.0", {"center": v(180.99, 99.5) * mm, "radius": 1.55 * mm});
            skCircle(sketch, "E158.46.1.0", {"center": v(177, 90) * mm, "radius": 11.8 * mm});
            skLineSegment(sketch, "E158.48.1.0", {"start": v(156.99, 83.86) * mm, "end": v(156.99, 76.51) * mm, "construction": true});
            skLineSegment(sketch, "E158.51.1.0", {"start": v(158.8, 80.5) * mm, "end": v(155, 80.5) * mm, "construction": true});
            skCircle(sketch, "E158.54.1.0", {"center": v(156.99, 80.5) * mm, "radius": 1.55 * mm});
            skLineSegment(sketch, "E158.0.1.1", {"start": v(177, 49) * mm, "end": v(161.5, 49) * mm, "construction": true});
            skLineSegment(sketch, "E158.3.1.1", {"start": v(177, 62) * mm, "end": v(177, 75) * mm, "construction": true});
            skLineSegment(sketch, "E158.6.1.1", {"start": v(156.44, 62) * mm, "end": v(181.62, 62) * mm, "construction": true});
            skCircle(sketch, "E158.9.1.1", {"center": v(177, 62) * mm, "radius": 11.8 * mm});
            skLineSegment(sketch, "E158.11.1.1", {"start": v(177, 50.2) * mm, "end": v(177, 104.46) * mm, "construction": true});
            skLineSegment(sketch, "E158.14.1.1", {"start": v(192.5, 62) * mm, "end": v(192.5, 49) * mm, "construction": true});
            skLineSegment(sketch, "E158.17.1.1", {"start": v(177, 62) * mm, "end": v(156.97, 62) * mm, "construction": true});
            skLineSegment(sketch, "E158.20.1.1", {"start": v(177, 75) * mm, "end": v(161.5, 75) * mm, "construction": true});
            skLineSegment(sketch, "E158.23.1.1", {"start": v(177, 75) * mm, "end": v(192.5, 75) * mm, "construction": true});
            skLineSegment(sketch, "E158.26.1.1", {"start": v(192.5, 62) * mm, "end": v(192.5, 75) * mm, "construction": true});
            skLineSegment(sketch, "E158.29.1.1", {"start": v(161.5, 62) * mm, "end": v(161.5, 75) * mm, "construction": true});
            skLineSegment(sketch, "E158.32.1.1", {"start": v(177, 49) * mm, "end": v(192.5, 49) * mm, "construction": true});
            skLineSegment(sketch, "E158.35.1.1", {"start": v(161.5, 62) * mm, "end": v(161.5, 49) * mm, "construction": true});
            skLineSegment(sketch, "E158.38.1.1", {"start": v(184.8, 71.5) * mm, "end": v(179, 71.5) * mm, "construction": true});
            skLineSegment(sketch, "E158.41.1.1", {"start": v(180.99, 74.86) * mm, "end": v(180.99, 68.38) * mm, "construction": true});
            skCircle(sketch, "E158.44.1.1", {"center": v(180.99, 71.5) * mm, "radius": 1.55 * mm});
            skCircle(sketch, "E158.46.1.1", {"center": v(177, 62) * mm, "radius": 11.8 * mm});
            skLineSegment(sketch, "E158.48.1.1", {"start": v(156.99, 55.86) * mm, "end": v(156.99, 48.51) * mm, "construction": true});
            skLineSegment(sketch, "E158.51.1.1", {"start": v(158.8, 52.5) * mm, "end": v(155, 52.5) * mm, "construction": true});
            skCircle(sketch, "E158.54.1.1", {"center": v(156.99, 52.5) * mm, "radius": 1.55 * mm});
            skSolve(sketch);
        }
        {
            var Q0;
            Q0=qCreatedBy(makeId("Top.planeOp"),FACE);
            var sketch = newSketch(context, id + "F6", { "sketchPlane" : qUnion([Q0])});
            skLineSegment(sketch, "E159.rect.bottom", {"start": v(149.9, 103.9) * mm, "end": v(112.5, 103.9) * mm});
            skLineSegment(sketch, "E159.rect.top", {"start": v(149.9, -73.9) * mm, "end": v(112.5, -73.9) * mm});
            skLineSegment(sketch, "E159.rect.left", {"start": v(149.9, 103.9) * mm, "end": v(149.9, 78) * mm});
            skLineSegment(sketch, "E159.rect.right", {"start": v(-154.9, 103.9) * mm, "end": v(-154.9, 78) * mm});
            skLineSegment(sketch, "E160.0", {"start": v(156.04, -80.04) * mm, "end": v(-161.04, -80.04) * mm, "construction": true});
            skLineSegment(sketch, "E161.0", {"start": v(156.04, 110.04) * mm, "end": v(156.04, -80.04) * mm, "construction": true});
            skLineSegment(sketch, "E162.0", {"start": v(-161.04, 110.04) * mm, "end": v(-161.04, -80.04) * mm, "construction": true});
            skLineSegment(sketch, "E163.0", {"start": v(156.04, 110.04) * mm, "end": v(-161.04, 110.04) * mm, "construction": true});
            skLineSegment(sketch, "E164.bottom", {"start": v(-17.5, -80.04) * mm, "end": v(-2.5, -80.04) * mm});
            skLineSegment(sketch, "E164.top", {"start": v(-17.5, -73.9) * mm, "end": v(-2.5, -73.9) * mm, "construction": true});
            skLineSegment(sketch, "E164.left", {"start": v(-17.5, -80.04) * mm, "end": v(-17.5, -73.9) * mm});
            skLineSegment(sketch, "E164.right", {"start": v(-2.5, -80.04) * mm, "end": v(-2.5, -73.9) * mm, "construction": true});
            skLineSegment(sketch, "E165.bottom", {"start": v(-117.5, -80.04) * mm, "end": v(-87.5, -80.04) * mm});
            skLineSegment(sketch, "E165.left", {"start": v(-117.5, -80.04) * mm, "end": v(-117.5, -73.9) * mm});
            skLineSegment(sketch, "E165.right", {"start": v(-87.5, -80.04) * mm, "end": v(-87.5, -73.9) * mm});
            skPoint(sketch, "E166", {"position": v(-102.5, -80.04) * mm});
            skLineSegment(sketch, "E167.bottom", {"start": v(-161.04, -48) * mm, "end": v(-154.9, -48) * mm});
            skLineSegment(sketch, "E167.top", {"start": v(-161.04, -18) * mm, "end": v(-154.9, -18) * mm});
            skLineSegment(sketch, "E167.left", {"start": v(-161.04, -48) * mm, "end": v(-161.04, -18) * mm});
            skPoint(sketch, "E168", {"position": v(-161.04, -33) * mm});
            skLineSegment(sketch, "E169.MirrorCS", {"start": v(156.04, -48) * mm, "end": v(149.9, -48) * mm});
            skLineSegment(sketch, "E170.MirrorCS", {"start": v(156.04, -48) * mm, "end": v(156.04, -18) * mm});
            skLineSegment(sketch, "E171.MirrorCS", {"start": v(156.04, -18) * mm, "end": v(149.9, -18) * mm});
            skLineSegment(sketch, "E172.MirrorCS", {"start": v(112.5, -80.04) * mm, "end": v(82.5, -80.04) * mm});
            skLineSegment(sketch, "E173.MirrorCS", {"start": v(82.5, -80.04) * mm, "end": v(82.5, -73.9) * mm});
            skLineSegment(sketch, "E174.MirrorCS", {"start": v(112.5, -80.04) * mm, "end": v(112.5, -73.9) * mm});
            skLineSegment(sketch, "E175.MirrorCS", {"start": v(12.5, -80.04) * mm, "end": v(12.5, -73.9) * mm});
            skLineSegment(sketch, "E176.MirrorCS", {"start": v(12.5, -80.04) * mm, "end": v(-2.5, -80.04) * mm});
            skLineSegment(sketch, "E177", {"start": v(-154.9, -18) * mm, "end": v(-154.9, -48) * mm, "construction": true});
            skLineSegment(sketch, "E178", {"start": v(-154.9, -48) * mm, "end": v(-154.9, -73.9) * mm});
            skLineSegment(sketch, "E179", {"start": v(-117.5, -73.9) * mm, "end": v(-154.9, -73.9) * mm});
            skLineSegment(sketch, "E180", {"start": v(-17.5, -73.9) * mm, "end": v(-87.5, -73.9) * mm});
            skLineSegment(sketch, "E181", {"start": v(82.5, -73.9) * mm, "end": v(12.5, -73.9) * mm});
            skLineSegment(sketch, "E182", {"start": v(149.9, -48) * mm, "end": v(149.9, -73.9) * mm});
            skLineSegment(sketch, "E183.MirrorCS", {"start": v(-161.04, 78) * mm, "end": v(-161.04, 48) * mm});
            skLineSegment(sketch, "E184.MirrorCS", {"start": v(-17.5, 110.04) * mm, "end": v(-17.5, 103.9) * mm});
            skLineSegment(sketch, "E185.MirrorCS", {"start": v(-17.5, 110.04) * mm, "end": v(-2.5, 110.04) * mm});
            skLineSegment(sketch, "E186.MirrorCS", {"start": v(12.5, 110.04) * mm, "end": v(12.5, 103.9) * mm});
            skLineSegment(sketch, "E187.MirrorCS", {"start": v(12.5, 110.04) * mm, "end": v(-2.5, 110.04) * mm});
            skLineSegment(sketch, "E188.MirrorCS", {"start": v(-117.5, 110.04) * mm, "end": v(-87.5, 110.04) * mm});
            skLineSegment(sketch, "E189.MirrorCS", {"start": v(-87.5, 110.04) * mm, "end": v(-87.5, 103.9) * mm});
            skLineSegment(sketch, "E190.MirrorCS", {"start": v(-117.5, 110.04) * mm, "end": v(-117.5, 103.9) * mm});
            skLineSegment(sketch, "E191.MirrorCS", {"start": v(82.5, 110.04) * mm, "end": v(82.5, 103.9) * mm});
            skLineSegment(sketch, "E192.MirrorCS", {"start": v(112.5, 110.04) * mm, "end": v(82.5, 110.04) * mm});
            skLineSegment(sketch, "E193.MirrorCS", {"start": v(112.5, 110.04) * mm, "end": v(112.5, 103.9) * mm});
            skLineSegment(sketch, "E194.MirrorCS", {"start": v(156.04, 78) * mm, "end": v(149.9, 78) * mm});
            skLineSegment(sketch, "E195.MirrorCS", {"start": v(156.04, 78) * mm, "end": v(156.04, 48) * mm});
            skLineSegment(sketch, "E196.MirrorCS", {"start": v(156.04, 48) * mm, "end": v(149.9, 48) * mm});
            skLineSegment(sketch, "E197", {"start": v(149.9, 48) * mm, "end": v(149.9, -18) * mm});
            skLineSegment(sketch, "E198", {"start": v(149.9, 78) * mm, "end": v(149.9, 48) * mm, "construction": true});
            skLineSegment(sketch, "E199", {"start": v(112.5, 103.9) * mm, "end": v(82.5, 103.9) * mm, "construction": true});
            skLineSegment(sketch, "E200", {"start": v(82.5, 103.9) * mm, "end": v(12.5, 103.9) * mm});
            skLineSegment(sketch, "E201", {"start": v(12.5, 103.9) * mm, "end": v(-17.5, 103.9) * mm, "construction": true});
            skLineSegment(sketch, "E202", {"start": v(-17.5, 103.9) * mm, "end": v(-87.5, 103.9) * mm});
            skLineSegment(sketch, "E203", {"start": v(-87.5, 103.9) * mm, "end": v(-117.5, 103.9) * mm, "construction": true});
            skLineSegment(sketch, "E204", {"start": v(-117.5, 103.9) * mm, "end": v(-154.9, 103.9) * mm});
            skLineSegment(sketch, "E205", {"start": v(-154.9, 78) * mm, "end": v(-154.9, 48) * mm, "construction": true});
            skLineSegment(sketch, "E206", {"start": v(-154.9, 48) * mm, "end": v(-154.9, -18) * mm});
            skLineSegment(sketch, "E207", {"start": v(149.9, 78) * mm, "end": v(149.9, 48) * mm});
            skLineSegment(sketch, "E208", {"start": v(-17.5, 103.9) * mm, "end": v(12.5, 103.9) * mm});
            skLineSegment(sketch, "E209", {"start": v(-87.5, 103.9) * mm, "end": v(-117.5, 103.9) * mm});
            skLineSegment(sketch, "E210", {"start": v(-154.9, 78) * mm, "end": v(-154.9, 48) * mm});
            skLineSegment(sketch, "E211", {"start": v(-154.9, -48) * mm, "end": v(-154.9, -18) * mm});
            skLineSegment(sketch, "E212", {"start": v(-117.5, -73.9) * mm, "end": v(-87.5, -73.9) * mm});
            skLineSegment(sketch, "E213", {"start": v(-17.5, -73.9) * mm, "end": v(12.5, -73.9) * mm});
            skLineSegment(sketch, "E214", {"start": v(82.5, -73.9) * mm, "end": v(112.5, -73.9) * mm});
            skLineSegment(sketch, "E215", {"start": v(149.9, -48) * mm, "end": v(149.9, -18) * mm});
            skLineSegment(sketch, "E216", {"start": v(82.5, 103.9) * mm, "end": v(112.5, 103.9) * mm});
            skLineSegment(sketch, "E217", {"start": v(-161.04, 15) * mm, "end": v(156.04, 15) * mm, "construction": true});
            skLineSegment(sketch, "E218", {"start": v(-2.5, 110.04) * mm, "end": v(-2.5, -80.04) * mm, "construction": true});
            skPoint(sketch, "E219", {"position": v(-2.5, 15) * mm});
            skLineSegment(sketch, "E220", {"start": v(-161.04, 48) * mm, "end": v(-154.9, 48) * mm});
            skLineSegment(sketch, "E221", {"start": v(-161.04, 78) * mm, "end": v(-154.9, 78) * mm});
            skPoint(sketch, "E222", {"position": v(-2.5, -73.9) * mm});
            skLineSegment(sketch, "E223.0", {"start": v(-242, 130) * mm, "end": v(-242, -184) * mm});
            skLineSegment(sketch, "E223.1", {"start": v(-217, 155) * mm, "end": v(222, 155) * mm});
            skLineSegment(sketch, "E224", {"start": v(-87.5, -77.82) * mm, "end": v(-17.5, -77.82) * mm, "construction": true});
            skPoint(sketch, "E225", {"position": v(-52.5, -77.82) * mm});
            skCircle(sketch, "E226", {"center": v(-52.51, -47.97) * mm, "radius": 0.25 * mm});
            skCircle(sketch, "E227.MirrorC", {"center": v(47.51, -47.97) * mm, "radius": 0.25 * mm});
            skCircle(sketch, "E228.MirrorC", {"center": v(-52.51, 77.97) * mm, "radius": 0.25 * mm});
            skCircle(sketch, "E229.MirrorC", {"center": v(47.51, 77.97) * mm, "radius": 0.25 * mm});
            skSolve(sketch);
        }
        {
            var Q0;
            Q0=qCreatedBy(makeId("Top.planeOp"),FACE);
            var sketch = newSketch(context, id + "F7", { "sketchPlane" : qUnion([Q0])});
            skLineSegment(sketch, "E230", {"start": v(-2.5, 198.56) * mm, "end": v(-2.5, -194.1) * mm, "construction": true});
            skLineSegment(sketch, "E231.bottom", {"start": v(-97.25, -56.75) * mm, "end": v(92.25, -56.75) * mm});
            skLineSegment(sketch, "E231.top", {"start": v(-97.25, 86.75) * mm, "end": v(92.25, 86.75) * mm});
            skLineSegment(sketch, "E231.left", {"start": v(-107.25, -46.75) * mm, "end": v(-107.25, 76.75) * mm});
            skLineSegment(sketch, "E231.right", {"start": v(102.25, -46.75) * mm, "end": v(102.25, 76.75) * mm});
            skPoint(sketch, "E232", {"position": v(-2.5, -56.75) * mm});
            skLineSegment(sketch, "E233", {"start": v(-132.25, 15) * mm, "end": v(127.25, 15) * mm, "construction": true});
            skPoint(sketch, "E234", {"position": v(-2.5, 15) * mm});
            skPoint(sketch, "E235.visualSharp", {"position": v(-107.25, 86.75) * mm});
            skArc(sketch, "E235.filletArc", {"start": v(-97.25, 86.75) * mm, "mid": v(-104.32, 83.82) * mm, "end": v(-107.25, 76.75) * mm});
            skPoint(sketch, "E236.visualSharp", {"position": v(-107.25, -56.75) * mm});
            skArc(sketch, "E236.filletArc", {"start": v(-107.25, -46.75) * mm, "mid": v(-104.32, -53.82) * mm, "end": v(-97.25, -56.75) * mm});
            skPoint(sketch, "E237.visualSharp", {"position": v(102.25, -56.75) * mm});
            skArc(sketch, "E237.filletArc", {"start": v(92.25, -56.75) * mm, "mid": v(99.32, -53.82) * mm, "end": v(102.25, -46.75) * mm});
            skPoint(sketch, "E238.visualSharp", {"position": v(102.25, 86.75) * mm});
            skArc(sketch, "E238.filletArc", {"start": v(102.25, 76.75) * mm, "mid": v(99.32, 83.82) * mm, "end": v(92.25, 86.75) * mm});
            skCircle(sketch, "E239", {"center": v(-2.5, 98.75) * mm, "radius": 1.55 * mm});
            skCircle(sketch, "E240", {"center": v(107.8, -62.3) * mm, "radius": 1.55 * mm});
            skCircle(sketch, "E241", {"center": v(-2.5, -68.75) * mm, "radius": 1.55 * mm});
            skArc(sketch, "E242.0", {"start": v(-132.25, -46.75) * mm, "mid": v(-122, -71.5) * mm, "end": v(-97.25, -81.75) * mm});
            skLineSegment(sketch, "E242.1", {"start": v(-132.25, -46.75) * mm, "end": v(-132.25, 76.75) * mm});
            skArc(sketch, "E242.2", {"start": v(-97.25, 111.75) * mm, "mid": v(-122, 101.5) * mm, "end": v(-132.25, 76.75) * mm});
            skLineSegment(sketch, "E242.3", {"start": v(-97.25, 111.75) * mm, "end": v(92.25, 111.75) * mm});
            skArc(sketch, "E242.4", {"start": v(127.25, 76.75) * mm, "mid": v(117, 101.5) * mm, "end": v(92.25, 111.75) * mm});
            skLineSegment(sketch, "E242.5", {"start": v(-97.25, -81.75) * mm, "end": v(92.25, -81.75) * mm});
            skLineSegment(sketch, "E242.6", {"start": v(127.25, -46.75) * mm, "end": v(127.25, 76.75) * mm});
            skArc(sketch, "E242.7", {"start": v(92.25, -81.75) * mm, "mid": v(117, -71.5) * mm, "end": v(127.25, -46.75) * mm});
            skPoint(sketch, "E243", {"position": v(-119.25, 15) * mm});
            skPoint(sketch, "E244.orphan", {"position": v(-107.25, 15) * mm});
            skPoint(sketch, "E245.orphan", {"position": v(102.25, 15) * mm});
            skCircle(sketch, "E246", {"center": v(114.25, 15) * mm, "radius": 1.55 * mm});
            skCircle(sketch, "E247", {"center": v(-119.25, 15) * mm, "radius": 1.55 * mm});
            skLineSegment(sketch, "E248", {"start": v(127.25, -46.75) * mm, "end": v(127.25, -81.75) * mm, "construction": true});
            skLineSegment(sketch, "E249", {"start": v(92.25, -81.75) * mm, "end": v(127.25, -81.75) * mm, "construction": true});
            skLineSegment(sketch, "E250", {"start": v(92.25, -46.75) * mm, "end": v(127.25, -81.75) * mm, "construction": true});
            skLineSegment(sketch, "E251", {"start": v(-97.25, -68.75) * mm, "end": v(-132.25, -68.75) * mm, "construction": true});
            skLineSegment(sketch, "E252", {"start": v(-119.25, -62.37) * mm, "end": v(-119.25, -81.75) * mm, "construction": true});
            skLineSegment(sketch, "E253", {"start": v(-97.25, -46.75) * mm, "end": v(-132.25, -81.75) * mm, "construction": true});
            skPoint(sketch, "E254", {"position": v(-119.25, -68.75) * mm});
            skPoint(sketch, "E255", {"position": v(-112.8, -62.3) * mm});
            skCircle(sketch, "E256.MirrorC", {"center": v(107.8, 92.3) * mm, "radius": 1.55 * mm});
            skArc(sketch, "E257.0", {"start": v(-119.25, -46.75) * mm, "mid": v(-112.8, -62.3) * mm, "end": v(-97.25, -68.75) * mm, "construction": true});
            skLineSegment(sketch, "E257.1", {"start": v(-119.25, -46.75) * mm, "end": v(-119.25, 76.75) * mm, "construction": true});
            skArc(sketch, "E257.2", {"start": v(-97.25, 98.75) * mm, "mid": v(-112.8, 92.3) * mm, "end": v(-119.25, 76.75) * mm, "construction": true});
            skLineSegment(sketch, "E257.3", {"start": v(-97.25, 98.75) * mm, "end": v(92.25, 98.75) * mm, "construction": true});
            skArc(sketch, "E257.4", {"start": v(114.25, 76.75) * mm, "mid": v(107.8, 92.3) * mm, "end": v(92.25, 98.75) * mm, "construction": true});
            skLineSegment(sketch, "E257.5", {"start": v(-97.25, -68.75) * mm, "end": v(92.25, -68.75) * mm, "construction": true});
            skLineSegment(sketch, "E257.6", {"start": v(114.25, -46.75) * mm, "end": v(114.25, 76.75) * mm, "construction": true});
            skArc(sketch, "E257.7", {"start": v(92.25, -68.75) * mm, "mid": v(107.8, -62.3) * mm, "end": v(114.25, -46.75) * mm, "construction": true});
            skPoint(sketch, "E258", {"position": v(-2.5, 86.75) * mm});
            skCircle(sketch, "E259", {"center": v(-112.8, -62.3) * mm, "radius": 1.55 * mm});
            skCircle(sketch, "E260.MirrorC", {"center": v(-112.8, 92.3) * mm, "radius": 1.55 * mm});
            skLineSegment(sketch, "E261", {"start": v(-97.25, -81.75) * mm, "end": v(-132.25, -81.75) * mm, "construction": true});
            skLineSegment(sketch, "E262", {"start": v(-132.25, -46.75) * mm, "end": v(-132.25, -81.75) * mm, "construction": true});
            skPoint(sketch, "E263", {"position": v(-132.25, -81.75) * mm});
            skLineSegment(sketch, "E264", {"start": v(114.25, -46.75) * mm, "end": v(114.25, -81.75) * mm, "construction": true});
            skLineSegment(sketch, "E265", {"start": v(92.25, -68.75) * mm, "end": v(127.25, -68.75) * mm, "construction": true});
            skLineSegment(sketch, "E266.0", {"start": v(-242, 130) * mm, "end": v(-242, -184) * mm});
            skLineSegment(sketch, "E266.1", {"start": v(-217, 155) * mm, "end": v(222, 155) * mm});
            skLineSegment(sketch, "E267.0", {"start": v(-17.5, -73.9) * mm, "end": v(-87.5, -73.9) * mm});
            skLineSegment(sketch, "E268", {"start": v(-87.5, -73.9) * mm, "end": v(-87.5, -81.75) * mm, "construction": true});
            skLineSegment(sketch, "E269.0", {"start": v(-17.5, -80.04) * mm, "end": v(-17.5, -73.9) * mm});
            skLineSegment(sketch, "E270.MirrorCS", {"start": v(127.25, 15) * mm, "end": v(-132.25, 15) * mm, "construction": true});
            skCircle(sketch, "E271.0", {"center": v(-52.51, -47.97) * mm, "radius": 0.25 * mm});
            skCircle(sketch, "E272.1", {"center": v(47.51, -47.97) * mm, "radius": 0.25 * mm});
            skCircle(sketch, "E273.0", {"center": v(47.51, 77.97) * mm, "radius": 0.25 * mm});
            skCircle(sketch, "E274.0", {"center": v(-52.51, 77.97) * mm, "radius": 0.25 * mm});
            skSolve(sketch);
        }
        {
            var Q0;
            Q0=qCreatedBy(makeId("Top.planeOp"),FACE);
            var sketch = newSketch(context, id + "F8", { "sketchPlane" : qUnion([Q0])});
            skLineSegment(sketch, "E275.0", {"start": v(-217, 155) * mm, "end": v(222, 155) * mm});
            skLineSegment(sketch, "E275.1", {"start": v(237, 140) * mm, "end": v(237, -184) * mm});
            skLineSegment(sketch, "E276.top", {"start": v(158.5, -60) * mm, "end": v(234.5, -60) * mm, "construction": true});
            skLineSegment(sketch, "E276.left", {"start": v(158.5, 5) * mm, "end": v(158.5, -60) * mm, "construction": true});
            skLineSegment(sketch, "E276.right", {"start": v(234.5, 20) * mm, "end": v(234.5, -60) * mm, "construction": true});
            skLineSegment(sketch, "E277.bottom", {"start": v(158.5, -60) * mm, "end": v(227.58, -60) * mm, "construction": true});
            skPoint(sketch, "E278.startSnap0", {"position": v(158.5, -33) * mm});
            skLineSegment(sketch, "E279.rect.bottom", {"start": v(199.5, -10.5) * mm, "end": v(187.5, -10.5) * mm});
            skLineSegment(sketch, "E279.rect.top", {"start": v(199.5, 10.5) * mm, "end": v(187.5, 10.5) * mm});
            skLineSegment(sketch, "E279.rect.left", {"start": v(199.5, -10.5) * mm, "end": v(199.5, 10.5) * mm});
            skLineSegment(sketch, "E279.rect.right", {"start": v(187.5, -10.5) * mm, "end": v(187.5, 10.5) * mm});
            skPoint(sketch, "E279.rect.middle", {"position": v(193.5, 0) * mm});
            skPoint(sketch, "E280", {"position": v(152.67, -33) * mm});
            skLineSegment(sketch, "E281", {"start": v(160.58, 5) * mm, "end": v(160.58, -60) * mm, "construction": true});
            skLineSegment(sketch, "E282", {"start": v(193.5, 10.5) * mm, "end": v(193.5, -60) * mm, "construction": true});
            skCircle(sketch, "E283", {"center": v(193.5, 10.5) * mm, "radius": 6 * mm});
            skLineSegment(sketch, "E284.left", {"start": v(234.5, -18) * mm, "end": v(234.5, -39) * mm});
            skLineSegment(sketch, "E284.right", {"start": v(237, -18) * mm, "end": v(237, -39) * mm});
            skLineSegment(sketch, "E285.right", {"start": v(158.54, -18) * mm, "end": v(158.54, -39) * mm});
            skLineSegment(sketch, "E285.left", {"start": v(156.04, -18) * mm, "end": v(156.04, -39) * mm});
            skLineSegment(sketch, "E285.top", {"start": v(156.04, -39) * mm, "end": v(158.54, -39) * mm});
            skLineSegment(sketch, "E284.bottom", {"start": v(234.5, -18) * mm, "end": v(237, -18) * mm});
            skLineSegment(sketch, "E284.top", {"start": v(234.5, -39) * mm, "end": v(237, -39) * mm});
            skLineSegment(sketch, "E285.bottom", {"start": v(156.04, -18) * mm, "end": v(158.54, -18) * mm});
            skSolve(sketch);
        }
        {
            var Q0;
            Q0=qCreatedBy(makeId("Top.planeOp"),FACE);
            var sketch = newSketch(context, id + "F9", { "sketchPlane" : qUnion([Q0])});
            skLineSegment(sketch, "E286.0", {"start": v(-217, 155) * mm, "end": v(222, 155) * mm});
            skLineSegment(sketch, "E286.2", {"start": v(237, 140) * mm, "end": v(237, -184) * mm});
            skLineSegment(sketch, "E286.4", {"start": v(-227, -199) * mm, "end": v(222, -199) * mm});
            skLineSegment(sketch, "E286.6", {"start": v(-242, 130) * mm, "end": v(-242, -184) * mm});
            skArc(sketch, "E286.7", {"start": v(-237, 135) * mm, "mid": v(-240.54, 133.54) * mm, "end": v(-242, 130) * mm});
            skLineSegment(sketch, "E286.8", {"start": v(-237, 135) * mm, "end": v(-232, 135) * mm});
            skArc(sketch, "E286.9", {"start": v(-232, 135) * mm, "mid": v(-224.93, 137.93) * mm, "end": v(-222, 145) * mm});
            skLineSegment(sketch, "E286.10", {"start": v(-222, 145) * mm, "end": v(-222, 150) * mm});
            skArc(sketch, "E286.11", {"start": v(-217, 155) * mm, "mid": v(-220.54, 153.54) * mm, "end": v(-222, 150) * mm});
            skCircle(sketch, "E286.13", {"center": v(-234.5, -22) * mm, "radius": 2.1 * mm});
            skCircle(sketch, "E286.14", {"center": v(168.5, 147.5) * mm, "radius": 2.1 * mm});
            skCircle(sketch, "E286.15", {"center": v(229.5, -22) * mm, "radius": 2.1 * mm});
            skCircle(sketch, "E286.16", {"center": v(168.5, -191.5) * mm, "radius": 2.1 * mm});
            skCircle(sketch, "E286.17", {"center": v(-173.5, -191.5) * mm, "radius": 2.1 * mm});
            skCircle(sketch, "E286.18", {"center": v(-173.5, 147.5) * mm, "radius": 2.1 * mm});
            skLineSegment(sketch, "E287.0.0", {"start": v(-21.64, -141.17) * mm, "end": v(-21.64, -116.17) * mm});
            skLineSegment(sketch, "E287.0.1", {"start": v(-21.64, -116.17) * mm, "end": v(-15.5, -116.17) * mm});
            skLineSegment(sketch, "E287.0.2", {"start": v(-15.5, -116.17) * mm, "end": v(-15.5, -96.17) * mm});
            skLineSegment(sketch, "E287.0.3", {"start": v(-15.5, -96.17) * mm, "end": v(-21.64, -96.17) * mm});
            skLineSegment(sketch, "E287.0.4", {"start": v(-21.64, -96.17) * mm, "end": v(-21.64, -71.17) * mm});
            skLineSegment(sketch, "E287.0.5", {"start": v(-21.64, -71.17) * mm, "end": v(-51.64, -71.17) * mm});
            skLineSegment(sketch, "E287.0.6", {"start": v(-51.64, -71.17) * mm, "end": v(-51.64, -65.03) * mm});
            skLineSegment(sketch, "E287.0.7", {"start": v(-51.64, -65.03) * mm, "end": v(-71.64, -65.03) * mm});
            skLineSegment(sketch, "E287.0.8", {"start": v(-71.64, -65.03) * mm, "end": v(-71.64, -71.17) * mm});
            skLineSegment(sketch, "E287.0.9", {"start": v(-71.64, -71.17) * mm, "end": v(-151.64, -71.17) * mm});
            skLineSegment(sketch, "E287.0.10", {"start": v(-151.64, -71.17) * mm, "end": v(-151.64, -65.03) * mm});
            skLineSegment(sketch, "E287.0.11", {"start": v(-151.64, -65.03) * mm, "end": v(-171.64, -65.03) * mm});
            skLineSegment(sketch, "E287.0.12", {"start": v(-171.64, -65.03) * mm, "end": v(-171.64, -71.17) * mm});
            skLineSegment(sketch, "E287.0.13", {"start": v(-171.64, -71.17) * mm, "end": v(-201.64, -71.17) * mm});
            skLineSegment(sketch, "E287.0.14", {"start": v(-201.64, -71.17) * mm, "end": v(-201.64, -96.17) * mm});
            skLineSegment(sketch, "E287.0.15", {"start": v(-201.64, -96.17) * mm, "end": v(-207.78, -96.17) * mm});
            skLineSegment(sketch, "E287.0.16", {"start": v(-207.78, -96.17) * mm, "end": v(-207.78, -116.17) * mm});
            skLineSegment(sketch, "E287.0.17", {"start": v(-207.78, -116.17) * mm, "end": v(-201.64, -116.17) * mm});
            skLineSegment(sketch, "E287.0.18", {"start": v(-201.64, -116.17) * mm, "end": v(-201.64, -141.17) * mm});
            skLineSegment(sketch, "E287.0.19", {"start": v(-201.64, -141.17) * mm, "end": v(-171.64, -141.17) * mm});
            skLineSegment(sketch, "E287.0.20", {"start": v(-171.64, -141.17) * mm, "end": v(-171.64, -147.3) * mm});
            skLineSegment(sketch, "E287.0.21", {"start": v(-171.64, -147.3) * mm, "end": v(-151.64, -147.3) * mm});
            skLineSegment(sketch, "E287.0.22", {"start": v(-151.64, -147.3) * mm, "end": v(-151.64, -141.17) * mm});
            skLineSegment(sketch, "E287.0.23", {"start": v(-151.64, -141.17) * mm, "end": v(-71.64, -141.17) * mm});
            skLineSegment(sketch, "E287.0.24", {"start": v(-71.64, -141.17) * mm, "end": v(-71.64, -147.3) * mm});
            skLineSegment(sketch, "E287.0.25", {"start": v(-71.64, -147.3) * mm, "end": v(-51.64, -147.3) * mm});
            skLineSegment(sketch, "E287.0.26", {"start": v(-51.64, -147.3) * mm, "end": v(-51.64, -141.17) * mm});
            skLineSegment(sketch, "E287.0.27", {"start": v(-51.64, -141.17) * mm, "end": v(-21.64, -141.17) * mm});
            skLineSegment(sketch, "E288.1.0", {"start": v(16.64, -71.17) * mm, "end": v(16.64, -96.17) * mm});
            skLineSegment(sketch, "E288.1.1", {"start": v(16.64, -96.17) * mm, "end": v(10.5, -96.17) * mm});
            skLineSegment(sketch, "E288.1.2", {"start": v(10.5, -96.17) * mm, "end": v(10.5, -116.17) * mm});
            skLineSegment(sketch, "E288.1.3", {"start": v(10.5, -116.17) * mm, "end": v(16.64, -116.17) * mm});
            skLineSegment(sketch, "E288.1.4", {"start": v(16.64, -116.17) * mm, "end": v(16.64, -141.17) * mm});
            skLineSegment(sketch, "E288.1.5", {"start": v(16.64, -141.17) * mm, "end": v(46.64, -141.17) * mm});
            skLineSegment(sketch, "E288.1.6", {"start": v(46.64, -141.17) * mm, "end": v(46.64, -147.3) * mm});
            skLineSegment(sketch, "E288.1.7", {"start": v(46.64, -147.3) * mm, "end": v(66.64, -147.3) * mm});
            skLineSegment(sketch, "E288.1.8", {"start": v(66.64, -147.3) * mm, "end": v(66.64, -141.17) * mm});
            skLineSegment(sketch, "E288.1.9", {"start": v(66.64, -141.17) * mm, "end": v(146.64, -141.17) * mm});
            skLineSegment(sketch, "E288.1.10", {"start": v(146.64, -141.17) * mm, "end": v(146.64, -147.3) * mm});
            skLineSegment(sketch, "E288.1.11", {"start": v(146.64, -147.3) * mm, "end": v(166.64, -147.3) * mm});
            skLineSegment(sketch, "E288.1.12", {"start": v(166.64, -147.3) * mm, "end": v(166.64, -141.17) * mm});
            skLineSegment(sketch, "E288.1.13", {"start": v(166.64, -141.17) * mm, "end": v(196.64, -141.17) * mm});
            skLineSegment(sketch, "E288.1.14", {"start": v(196.64, -141.17) * mm, "end": v(196.64, -116.17) * mm});
            skLineSegment(sketch, "E288.1.15", {"start": v(196.64, -116.17) * mm, "end": v(202.78, -116.17) * mm});
            skLineSegment(sketch, "E288.1.16", {"start": v(202.78, -116.17) * mm, "end": v(202.78, -96.17) * mm});
            skLineSegment(sketch, "E288.1.17", {"start": v(202.78, -96.17) * mm, "end": v(196.64, -96.17) * mm});
            skLineSegment(sketch, "E288.1.18", {"start": v(196.64, -96.17) * mm, "end": v(196.64, -71.17) * mm});
            skLineSegment(sketch, "E288.1.19", {"start": v(196.64, -71.17) * mm, "end": v(166.64, -71.17) * mm});
            skLineSegment(sketch, "E288.1.20", {"start": v(166.64, -71.17) * mm, "end": v(166.64, -65.03) * mm});
            skLineSegment(sketch, "E288.1.21", {"start": v(166.64, -65.03) * mm, "end": v(146.64, -65.03) * mm});
            skLineSegment(sketch, "E288.1.22", {"start": v(146.64, -65.03) * mm, "end": v(146.64, -71.17) * mm});
            skLineSegment(sketch, "E288.1.23", {"start": v(146.64, -71.17) * mm, "end": v(66.64, -71.17) * mm});
            skLineSegment(sketch, "E288.1.24", {"start": v(66.64, -71.17) * mm, "end": v(66.64, -65.03) * mm});
            skLineSegment(sketch, "E288.1.25", {"start": v(66.64, -65.03) * mm, "end": v(46.64, -65.03) * mm});
            skLineSegment(sketch, "E288.1.26", {"start": v(46.64, -65.03) * mm, "end": v(46.64, -71.17) * mm});
            skLineSegment(sketch, "E288.1.27", {"start": v(46.64, -71.17) * mm, "end": v(16.64, -71.17) * mm});
            skArc(sketch, "E289.0", {"start": v(-216.6, 102.2) * mm, "mid": v(-213.41, 97.33) * mm, "end": v(-208.05, 95.06) * mm});
            skLineSegment(sketch, "E289.1", {"start": v(-217.3, 102.2) * mm, "end": v(-217.3, 107.8) * mm});
            skArc(sketch, "E289.2", {"start": v(-208.05, 114.94) * mm, "mid": v(-213.41, 112.67) * mm, "end": v(-216.6, 107.8) * mm});
            skArc(sketch, "E289.3", {"start": v(-197.4, 107.8) * mm, "mid": v(-200.59, 112.67) * mm, "end": v(-205.95, 114.94) * mm});
            skArc(sketch, "E289.4", {"start": v(-205.95, 95.06) * mm, "mid": v(-200.59, 97.33) * mm, "end": v(-197.4, 102.2) * mm});
            skLineSegment(sketch, "E290.0", {"start": v(-216.6, 107.8) * mm, "end": v(-217.3, 107.8) * mm});
            skLineSegment(sketch, "E290.1", {"start": v(-216.6, 102.2) * mm, "end": v(-217.3, 102.2) * mm});
            skLineSegment(sketch, "E291.2", {"start": v(-197.4, 107.8) * mm, "end": v(-196.7, 107.8) * mm});
            skLineSegment(sketch, "E291.3", {"start": v(-196.7, 102.2) * mm, "end": v(-197.4, 102.2) * mm});
            skLineSegment(sketch, "E291.4", {"start": v(-196.7, 102.2) * mm, "end": v(-196.7, 107.8) * mm});
            skLineSegment(sketch, "E292.0", {"start": v(-208.05, 114.94) * mm, "end": v(-208.05, 116) * mm});
            skLineSegment(sketch, "E292.1", {"start": v(-205.95, 116) * mm, "end": v(-208.05, 116) * mm});
            skLineSegment(sketch, "E292.2", {"start": v(-205.95, 114.94) * mm, "end": v(-205.95, 116) * mm});
            skArc(sketch, "E293.0", {"start": v(-208.05, 88.94) * mm, "mid": v(-213.41, 86.67) * mm, "end": v(-216.6, 81.8) * mm});
            skArc(sketch, "E293.1", {"start": v(-197.4, 81.8) * mm, "mid": v(-200.59, 86.67) * mm, "end": v(-205.95, 88.94) * mm});
            skArc(sketch, "E293.2", {"start": v(-205.95, 69.06) * mm, "mid": v(-200.59, 71.33) * mm, "end": v(-197.4, 76.2) * mm});
            skArc(sketch, "E293.3", {"start": v(-216.6, 76.2) * mm, "mid": v(-213.41, 71.33) * mm, "end": v(-208.05, 69.06) * mm});
            skLineSegment(sketch, "E293.4", {"start": v(-217.3, 76.2) * mm, "end": v(-217.3, 81.8) * mm});
            skLineSegment(sketch, "E293.5", {"start": v(-196.7, 76.2) * mm, "end": v(-196.7, 81.8) * mm});
            skLineSegment(sketch, "E293.6", {"start": v(-205.95, 90) * mm, "end": v(-208.05, 90) * mm});
            skLineSegment(sketch, "E293.7", {"start": v(-205.95, 68) * mm, "end": v(-208.05, 68) * mm});
            skLineSegment(sketch, "E293.8", {"start": v(-205.95, 69.06) * mm, "end": v(-205.95, 68) * mm});
            skLineSegment(sketch, "E293.9", {"start": v(-208.05, 69.06) * mm, "end": v(-208.05, 68) * mm});
            skLineSegment(sketch, "E293.10", {"start": v(-208.05, 88.94) * mm, "end": v(-208.05, 90) * mm});
            skLineSegment(sketch, "E293.11", {"start": v(-205.95, 88.94) * mm, "end": v(-205.95, 90) * mm});
            skLineSegment(sketch, "E293.12", {"start": v(-216.6, 81.8) * mm, "end": v(-217.3, 81.8) * mm});
            skLineSegment(sketch, "E293.13", {"start": v(-197.4, 81.8) * mm, "end": v(-196.7, 81.8) * mm});
            skLineSegment(sketch, "E293.14", {"start": v(-196.7, 76.2) * mm, "end": v(-197.4, 76.2) * mm});
            skLineSegment(sketch, "E293.15", {"start": v(-216.6, 76.2) * mm, "end": v(-217.3, 76.2) * mm});
            skArc(sketch, "E294.0", {"start": v(-205.95, 43.06) * mm, "mid": v(-200.59, 45.33) * mm, "end": v(-197.4, 50.2) * mm});
            skArc(sketch, "E294.1", {"start": v(-208.05, 62.94) * mm, "mid": v(-213.41, 60.67) * mm, "end": v(-216.6, 55.8) * mm});
            skArc(sketch, "E294.2", {"start": v(-216.6, 50.2) * mm, "mid": v(-213.41, 45.33) * mm, "end": v(-208.05, 43.06) * mm});
            skArc(sketch, "E294.3", {"start": v(-197.4, 55.8) * mm, "mid": v(-200.59, 60.67) * mm, "end": v(-205.95, 62.94) * mm});
            skArc(sketch, "E294.4", {"start": v(-208.05, 36.94) * mm, "mid": v(-213.41, 34.67) * mm, "end": v(-216.6, 29.8) * mm});
            skArc(sketch, "E294.5", {"start": v(-197.4, 29.8) * mm, "mid": v(-200.59, 34.67) * mm, "end": v(-205.95, 36.94) * mm});
            skArc(sketch, "E294.6", {"start": v(-205.95, 17.06) * mm, "mid": v(-200.59, 19.33) * mm, "end": v(-197.4, 24.2) * mm});
            skArc(sketch, "E294.7", {"start": v(-216.6, 24.2) * mm, "mid": v(-213.41, 19.33) * mm, "end": v(-208.05, 17.06) * mm});
            skLineSegment(sketch, "E295.0", {"start": v(-217.3, 50.2) * mm, "end": v(-217.3, 55.8) * mm});
            skLineSegment(sketch, "E295.1", {"start": v(-196.7, 50.2) * mm, "end": v(-196.7, 55.8) * mm});
            skLineSegment(sketch, "E295.2", {"start": v(-217.3, 24.2) * mm, "end": v(-217.3, 29.8) * mm});
            skLineSegment(sketch, "E295.3", {"start": v(-196.7, 24.2) * mm, "end": v(-196.7, 29.8) * mm});
            skLineSegment(sketch, "E296.0", {"start": v(-208.05, 62.94) * mm, "end": v(-208.05, 64) * mm});
            skLineSegment(sketch, "E296.1", {"start": v(-205.95, 64) * mm, "end": v(-208.05, 64) * mm});
            skLineSegment(sketch, "E296.2", {"start": v(-205.95, 62.94) * mm, "end": v(-205.95, 64) * mm});
            skLineSegment(sketch, "E296.3", {"start": v(-216.6, 50.2) * mm, "end": v(-217.3, 50.2) * mm});
            skLineSegment(sketch, "E296.4", {"start": v(-216.6, 55.8) * mm, "end": v(-217.3, 55.8) * mm});
            skLineSegment(sketch, "E296.5", {"start": v(-197.4, 55.8) * mm, "end": v(-196.7, 55.8) * mm});
            skLineSegment(sketch, "E296.6", {"start": v(-196.7, 50.2) * mm, "end": v(-197.4, 50.2) * mm});
            skLineSegment(sketch, "E297.0", {"start": v(-208.05, 43.06) * mm, "end": v(-208.05, 42) * mm});
            skLineSegment(sketch, "E297.1", {"start": v(-205.95, 42) * mm, "end": v(-208.05, 42) * mm});
            skLineSegment(sketch, "E297.2", {"start": v(-205.95, 43.06) * mm, "end": v(-205.95, 42) * mm});
            skLineSegment(sketch, "E297.3", {"start": v(-208.05, 36.94) * mm, "end": v(-208.05, 38) * mm});
            skLineSegment(sketch, "E297.4", {"start": v(-205.95, 38) * mm, "end": v(-208.05, 38) * mm});
            skLineSegment(sketch, "E297.5", {"start": v(-205.95, 36.94) * mm, "end": v(-205.95, 38) * mm});
            skLineSegment(sketch, "E298.0", {"start": v(-216.6, 29.8) * mm, "end": v(-217.3, 29.8) * mm});
            skLineSegment(sketch, "E298.1", {"start": v(-216.6, 24.2) * mm, "end": v(-217.3, 24.2) * mm});
            skLineSegment(sketch, "E298.2", {"start": v(-196.7, 24.2) * mm, "end": v(-197.4, 24.2) * mm});
            skLineSegment(sketch, "E298.3", {"start": v(-197.4, 29.8) * mm, "end": v(-196.7, 29.8) * mm});
            skLineSegment(sketch, "E299.0", {"start": v(-208.05, 17.06) * mm, "end": v(-208.05, 16) * mm});
            skLineSegment(sketch, "E299.1", {"start": v(-205.95, 16) * mm, "end": v(-208.05, 16) * mm});
            skLineSegment(sketch, "E299.2", {"start": v(-205.95, 17.06) * mm, "end": v(-205.95, 16) * mm});
            skCircle(sketch, "E300.0", {"center": v(217, 90) * mm, "radius": 11.8 * mm});
            skCircle(sketch, "E300.1", {"center": v(217, 62) * mm, "radius": 11.8 * mm});
            skCircle(sketch, "E300.2", {"center": v(217, 125) * mm, "radius": 9.75 * mm});
            skCircle(sketch, "E301.0", {"center": v(196.99, 80.5) * mm, "radius": 1.55 * mm});
            skCircle(sketch, "E301.1", {"center": v(196.99, 52.5) * mm, "radius": 1.55 * mm});
            skCircle(sketch, "E301.2", {"center": v(204.5, 125) * mm, "radius": 1.75 * mm});
            skCircle(sketch, "E301.3", {"center": v(223.25, 135.83) * mm, "radius": 1.75 * mm});
            skCircle(sketch, "E301.4", {"center": v(223.25, 114.17) * mm, "radius": 1.75 * mm});
            skCircle(sketch, "E301.5", {"center": v(220.99, 71.5) * mm, "radius": 1.55 * mm});
            skCircle(sketch, "E301.6", {"center": v(220.99, 99.5) * mm, "radius": 1.55 * mm});
            skLineSegment(sketch, "E302.0.0", {"start": v(149.9, 78) * mm, "end": v(149.9, 103.9) * mm});
            skLineSegment(sketch, "E302.0.1", {"start": v(149.9, 103.9) * mm, "end": v(112.5, 103.9) * mm});
            skLineSegment(sketch, "E302.0.2", {"start": v(112.5, 103.9) * mm, "end": v(82.5, 103.9) * mm});
            skLineSegment(sketch, "E302.0.3", {"start": v(82.5, 103.9) * mm, "end": v(12.5, 103.9) * mm});
            skLineSegment(sketch, "E302.0.4", {"start": v(12.5, 103.9) * mm, "end": v(-17.5, 103.9) * mm});
            skLineSegment(sketch, "E302.0.5", {"start": v(-17.5, 103.9) * mm, "end": v(-87.5, 103.9) * mm});
            skLineSegment(sketch, "E302.0.6", {"start": v(-87.5, 103.9) * mm, "end": v(-117.5, 103.9) * mm});
            skLineSegment(sketch, "E302.0.7", {"start": v(-117.5, 103.9) * mm, "end": v(-154.9, 103.9) * mm});
            skLineSegment(sketch, "E302.0.8", {"start": v(-154.9, 103.9) * mm, "end": v(-154.9, 78) * mm});
            skLineSegment(sketch, "E302.0.13", {"start": v(-154.9, -18) * mm, "end": v(-154.9, -48) * mm});
            skLineSegment(sketch, "E302.0.14", {"start": v(-154.9, -48) * mm, "end": v(-154.9, -73.9) * mm});
            skLineSegment(sketch, "E302.0.15", {"start": v(-154.9, -73.9) * mm, "end": v(-117.5, -73.9) * mm});
            skLineSegment(sketch, "E302.0.16", {"start": v(-117.5, -73.9) * mm, "end": v(-87.5, -73.9) * mm});
            skLineSegment(sketch, "E302.0.17", {"start": v(-87.5, -73.9) * mm, "end": v(-17.5, -73.9) * mm});
            skLineSegment(sketch, "E302.0.18", {"start": v(-17.5, -73.9) * mm, "end": v(12.5, -73.9) * mm});
            skLineSegment(sketch, "E302.0.19", {"start": v(12.5, -73.9) * mm, "end": v(82.5, -73.9) * mm});
            skLineSegment(sketch, "E302.0.20", {"start": v(82.5, -73.9) * mm, "end": v(112.5, -73.9) * mm});
            skLineSegment(sketch, "E302.0.21", {"start": v(112.5, -73.9) * mm, "end": v(149.9, -73.9) * mm});
            skLineSegment(sketch, "E302.0.22", {"start": v(149.9, -73.9) * mm, "end": v(149.9, -48) * mm});
            skLineSegment(sketch, "E302.0.23", {"start": v(149.9, -48) * mm, "end": v(149.9, -18) * mm});
            skLineSegment(sketch, "E302.0.24", {"start": v(149.9, -18) * mm, "end": v(149.9, 48) * mm});
            skLineSegment(sketch, "E302.0.25", {"start": v(149.9, 48) * mm, "end": v(149.9, 78) * mm});
            skLineSegment(sketch, "E302.1.0", {"start": v(-161.04, -18) * mm, "end": v(-161.04, -48) * mm});
            skLineSegment(sketch, "E302.1.1", {"start": v(-161.04, -48) * mm, "end": v(-154.9, -48) * mm});
            skLineSegment(sketch, "E302.1.2", {"start": v(-154.9, -48) * mm, "end": v(-154.9, -18) * mm});
            skLineSegment(sketch, "E302.1.3", {"start": v(-154.9, -18) * mm, "end": v(-161.04, -18) * mm});
            skLineSegment(sketch, "E302.2.0", {"start": v(-117.5, -73.9) * mm, "end": v(-117.5, -80.04) * mm});
            skLineSegment(sketch, "E302.2.1", {"start": v(-117.5, -80.04) * mm, "end": v(-87.5, -80.04) * mm});
            skLineSegment(sketch, "E302.2.2", {"start": v(-87.5, -80.04) * mm, "end": v(-87.5, -73.9) * mm});
            skLineSegment(sketch, "E302.2.3", {"start": v(-87.5, -73.9) * mm, "end": v(-117.5, -73.9) * mm});
            skLineSegment(sketch, "E302.3.0", {"start": v(-17.5, -73.9) * mm, "end": v(-17.5, -80.04) * mm});
            skLineSegment(sketch, "E302.3.1", {"start": v(-17.5, -80.04) * mm, "end": v(-2.5, -80.04) * mm});
            skLineSegment(sketch, "E302.3.2", {"start": v(-2.5, -80.04) * mm, "end": v(12.5, -80.04) * mm});
            skLineSegment(sketch, "E302.3.3", {"start": v(12.5, -80.04) * mm, "end": v(12.5, -73.9) * mm});
            skLineSegment(sketch, "E302.3.4", {"start": v(12.5, -73.9) * mm, "end": v(-17.5, -73.9) * mm});
            skLineSegment(sketch, "E302.4.0", {"start": v(82.5, -80.04) * mm, "end": v(112.5, -80.04) * mm});
            skLineSegment(sketch, "E302.4.1", {"start": v(112.5, -80.04) * mm, "end": v(112.5, -73.9) * mm});
            skLineSegment(sketch, "E302.4.2", {"start": v(112.5, -73.9) * mm, "end": v(82.5, -73.9) * mm});
            skLineSegment(sketch, "E302.4.3", {"start": v(82.5, -73.9) * mm, "end": v(82.5, -80.04) * mm});
            skLineSegment(sketch, "E302.5.0", {"start": v(149.9, -48) * mm, "end": v(156.04, -48) * mm});
            skLineSegment(sketch, "E302.5.1", {"start": v(156.04, -48) * mm, "end": v(156.04, -18) * mm});
            skLineSegment(sketch, "E302.5.2", {"start": v(156.04, -18) * mm, "end": v(149.9, -18) * mm});
            skLineSegment(sketch, "E302.5.3", {"start": v(149.9, -18) * mm, "end": v(149.9, -48) * mm});
            skLineSegment(sketch, "E302.6.0", {"start": v(156.04, 48) * mm, "end": v(156.04, 78) * mm});
            skLineSegment(sketch, "E302.6.1", {"start": v(156.04, 78) * mm, "end": v(149.9, 78) * mm});
            skLineSegment(sketch, "E302.6.2", {"start": v(149.9, 78) * mm, "end": v(149.9, 48) * mm});
            skLineSegment(sketch, "E302.6.3", {"start": v(149.9, 48) * mm, "end": v(156.04, 48) * mm});
            skLineSegment(sketch, "E302.7.0", {"start": v(112.5, 110.04) * mm, "end": v(82.5, 110.04) * mm});
            skLineSegment(sketch, "E302.7.1", {"start": v(82.5, 110.04) * mm, "end": v(82.5, 103.9) * mm});
            skLineSegment(sketch, "E302.7.2", {"start": v(82.5, 103.9) * mm, "end": v(112.5, 103.9) * mm});
            skLineSegment(sketch, "E302.7.3", {"start": v(112.5, 103.9) * mm, "end": v(112.5, 110.04) * mm});
            skLineSegment(sketch, "E302.8.0", {"start": v(-2.5, 110.04) * mm, "end": v(-17.5, 110.04) * mm});
            skLineSegment(sketch, "E302.8.1", {"start": v(-17.5, 110.04) * mm, "end": v(-17.5, 103.9) * mm});
            skLineSegment(sketch, "E302.8.2", {"start": v(-17.5, 103.9) * mm, "end": v(12.5, 103.9) * mm});
            skLineSegment(sketch, "E302.8.3", {"start": v(12.5, 103.9) * mm, "end": v(12.5, 110.04) * mm});
            skLineSegment(sketch, "E302.8.4", {"start": v(12.5, 110.04) * mm, "end": v(-2.5, 110.04) * mm});
            skLineSegment(sketch, "E302.9.0", {"start": v(-87.5, 110.04) * mm, "end": v(-117.5, 110.04) * mm});
            skLineSegment(sketch, "E302.9.1", {"start": v(-117.5, 110.04) * mm, "end": v(-117.5, 103.9) * mm});
            skLineSegment(sketch, "E302.9.2", {"start": v(-117.5, 103.9) * mm, "end": v(-87.5, 103.9) * mm});
            skLineSegment(sketch, "E302.9.3", {"start": v(-87.5, 103.9) * mm, "end": v(-87.5, 110.04) * mm});
            skLineSegment(sketch, "E303.0", {"start": v(-161.04, 48) * mm, "end": v(-154.9, 48) * mm});
            skLineSegment(sketch, "E303.1", {"start": v(-161.04, 78) * mm, "end": v(-161.04, 48) * mm});
            skLineSegment(sketch, "E303.3", {"start": v(-161.04, 78) * mm, "end": v(-154.9, 78) * mm});
            skLineSegment(sketch, "E304.0", {"start": v(-154.9, 48) * mm, "end": v(-154.9, -18) * mm});
            skLineSegment(sketch, "E304.1", {"start": v(-154.9, 78) * mm, "end": v(-154.9, 48) * mm});
            skLineSegment(sketch, "E305.0", {"start": v(-208.05, 95.06) * mm, "end": v(-208.05, 94) * mm});
            skLineSegment(sketch, "E305.1", {"start": v(-205.95, 94) * mm, "end": v(-208.05, 94) * mm});
            skLineSegment(sketch, "E305.2", {"start": v(-205.95, 95.06) * mm, "end": v(-205.95, 94) * mm});
            skCircle(sketch, "E306.0", {"center": v(107.8, 92.3) * mm, "radius": 1.55 * mm});
            skCircle(sketch, "E306.1", {"center": v(-2.5, 98.75) * mm, "radius": 1.55 * mm});
            skCircle(sketch, "E306.2", {"center": v(-112.8, 92.3) * mm, "radius": 1.55 * mm});
            skCircle(sketch, "E306.3", {"center": v(-119.25, 15) * mm, "radius": 1.55 * mm});
            skCircle(sketch, "E306.4", {"center": v(-112.8, -62.3) * mm, "radius": 1.55 * mm});
            skCircle(sketch, "E306.5", {"center": v(-2.5, -68.75) * mm, "radius": 1.55 * mm});
            skCircle(sketch, "E306.6", {"center": v(107.8, -62.3) * mm, "radius": 1.55 * mm});
            skCircle(sketch, "E306.7", {"center": v(114.25, 15) * mm, "radius": 1.55 * mm});
            skLineSegment(sketch, "E307.0", {"start": v(-234, -75) * mm, "end": v(-164, -75) * mm});
            skLineSegment(sketch, "E307.1", {"start": v(-234, -36) * mm, "end": v(-234, -75) * mm});
            skLineSegment(sketch, "E307.2", {"start": v(-234, -36) * mm, "end": v(-164, -36) * mm});
            skLineSegment(sketch, "E307.3", {"start": v(-164, -36) * mm, "end": v(-164, -75) * mm});
            skLineSegment(sketch, "E308.0", {"start": v(187.5, -10.5) * mm, "end": v(187.5, 10.5) * mm});
            skCircle(sketch, "E308.1", {"center": v(193.5, 10.5) * mm, "radius": 6 * mm});
            skLineSegment(sketch, "E308.2", {"start": v(199.5, -10.5) * mm, "end": v(199.5, 10.5) * mm});
            skLineSegment(sketch, "E308.3", {"start": v(199.5, -10.5) * mm, "end": v(187.5, -10.5) * mm});
            skLineSegment(sketch, "E309.0", {"start": v(156.04, -39) * mm, "end": v(158.54, -39) * mm});
            skLineSegment(sketch, "E309.1", {"start": v(158.54, -18) * mm, "end": v(158.54, -39) * mm});
            skLineSegment(sketch, "E309.2", {"start": v(156.04, -18) * mm, "end": v(158.54, -18) * mm});
            skLineSegment(sketch, "E310.0.0", {"start": v(158.54, -39) * mm, "end": v(158.54, -18) * mm});
            skLineSegment(sketch, "E310.0.1", {"start": v(158.54, -18) * mm, "end": v(156.04, -18) * mm});
            skLineSegment(sketch, "E310.0.2", {"start": v(156.04, -18) * mm, "end": v(156.04, -39) * mm});
            skLineSegment(sketch, "E311.0", {"start": v(234.5, -18) * mm, "end": v(234.5, -39) * mm});
            skLineSegment(sketch, "E312.0", {"start": v(234.5, -18) * mm, "end": v(237, -18) * mm});
            skLineSegment(sketch, "E313.0", {"start": v(234.5, -39) * mm, "end": v(237, -39) * mm});
            skLineSegment(sketch, "E314.0.0", {"start": v(237, 140) * mm, "end": v(237, 140) * mm});
            skLineSegment(sketch, "E314.0.2", {"start": v(214.5, 155) * mm, "end": v(-217, 155) * mm});
            skLineSegment(sketch, "E314.0.4", {"start": v(-222, 150) * mm, "end": v(-222, 145) * mm});
            skArc(sketch, "E314.0.5", {"start": v(-222, 145) * mm, "mid": v(-224.93, 137.93) * mm, "end": v(-232, 135) * mm});
            skLineSegment(sketch, "E314.0.6", {"start": v(-232, 135) * mm, "end": v(-237, 135) * mm});
            skLineSegment(sketch, "E314.0.8", {"start": v(-242, 130) * mm, "end": v(-242, 130) * mm});
            skLineSegment(sketch, "E314.0.10", {"start": v(-234.5, -199) * mm, "end": v(-227, -199) * mm, "construction": true});
            skCircle(sketch, "E315.0", {"center": v(177, 90) * mm, "radius": 11.8 * mm});
            skCircle(sketch, "E315.1", {"center": v(177, 62) * mm, "radius": 11.8 * mm});
            skCircle(sketch, "E315.2", {"center": v(156.99, 52.5) * mm, "radius": 1.55 * mm});
            skCircle(sketch, "E315.3", {"center": v(156.99, 80.5) * mm, "radius": 1.55 * mm});
            skCircle(sketch, "E315.4", {"center": v(180.99, 71.5) * mm, "radius": 1.55 * mm});
            skCircle(sketch, "E315.5", {"center": v(180.99, 99.5) * mm, "radius": 1.55 * mm});
            skArc(sketch, "E316.0", {"start": v(222, -199) * mm, "mid": v(232.6, -194.6) * mm, "end": v(237, -184) * mm});
            skArc(sketch, "E317.0", {"start": v(-242, -184) * mm, "mid": v(-237.6, -194.6) * mm, "end": v(-227, -199) * mm});
            skArc(sketch, "E318.0", {"start": v(237, 140) * mm, "mid": v(232.6, 150.6) * mm, "end": v(222, 155) * mm});
            skCircle(sketch, "E319.0", {"center": v(-52.51, -47.97) * mm, "radius": 0.25 * mm});
            skCircle(sketch, "E319.1", {"center": v(47.51, -47.97) * mm, "radius": 0.25 * mm});
            skCircle(sketch, "E319.2", {"center": v(47.51, 77.97) * mm, "radius": 0.25 * mm});
            skCircle(sketch, "E319.3", {"center": v(-52.51, 77.97) * mm, "radius": 0.25 * mm});
            skSolve(sketch);
        }
        {
            var Q0;
            Q0=makeQuery(id+"F9.imprint","IMPRINT",FACE,{"disambiguationData":[TD([[makeQuery(id+"F9.imprint","IMPRINT",EDGE,{"derivedFrom":sQuery(id+"F9.wireOp",EDGE,"E286.13")}),-1.0]])]});
            extrude(context, id + "F10", {"entities" : qUnion([Q0]), "oppositeDirection" : true, "depth" : (getVariable(context, 'PanelThickness')) * mm});
        }
        {
            var Q0;
            Q0=qCreatedBy(makeId("Top.planeOp"),FACE);
            var sketch = newSketch(context, id + "F11", { "sketchPlane" : qUnion([Q0])});
            skLineSegment(sketch, "E320.0", {"start": v(-97.25, -56.75) * mm, "end": v(92.25, -56.75) * mm});
            skLineSegment(sketch, "E320.1", {"start": v(-97.25, 86.75) * mm, "end": v(92.25, 86.75) * mm});
            skArc(sketch, "E320.2", {"start": v(-97.25, 86.75) * mm, "mid": v(-104.32, 83.82) * mm, "end": v(-107.25, 76.75) * mm});
            skLineSegment(sketch, "E320.3", {"start": v(-107.25, -46.75) * mm, "end": v(-107.25, 76.75) * mm});
            skArc(sketch, "E320.4", {"start": v(-107.25, -46.75) * mm, "mid": v(-104.32, -53.82) * mm, "end": v(-97.25, -56.75) * mm});
            skArc(sketch, "E320.5", {"start": v(92.25, -56.75) * mm, "mid": v(99.32, -53.82) * mm, "end": v(102.25, -46.75) * mm});
            skLineSegment(sketch, "E320.6", {"start": v(102.25, -46.75) * mm, "end": v(102.25, 76.75) * mm});
            skArc(sketch, "E320.7", {"start": v(102.25, 76.75) * mm, "mid": v(99.32, 83.82) * mm, "end": v(92.25, 86.75) * mm});
            skLineSegment(sketch, "E321.0", {"start": v(-132.25, -46.75) * mm, "end": v(-132.25, 76.75) * mm});
            skArc(sketch, "E321.1", {"start": v(-97.25, 111.75) * mm, "mid": v(-122, 101.5) * mm, "end": v(-132.25, 76.75) * mm});
            skArc(sketch, "E321.2", {"start": v(-132.25, -46.75) * mm, "mid": v(-122, -71.5) * mm, "end": v(-97.25, -81.75) * mm});
            skLineSegment(sketch, "E321.3", {"start": v(-97.25, -81.75) * mm, "end": v(92.25, -81.75) * mm});
            skArc(sketch, "E321.4", {"start": v(92.25, -81.75) * mm, "mid": v(117, -71.5) * mm, "end": v(127.25, -46.75) * mm});
            skLineSegment(sketch, "E321.5", {"start": v(127.25, -46.75) * mm, "end": v(127.25, 76.75) * mm});
            skArc(sketch, "E321.6", {"start": v(127.25, 76.75) * mm, "mid": v(117, 101.5) * mm, "end": v(92.25, 111.75) * mm});
            skLineSegment(sketch, "E321.7", {"start": v(-97.25, 111.75) * mm, "end": v(92.25, 111.75) * mm});
            skCircle(sketch, "E322.0", {"center": v(-112.8, 92.3) * mm, "radius": 1.55 * mm});
            skCircle(sketch, "E322.1", {"center": v(-119.25, 15) * mm, "radius": 1.55 * mm});
            skCircle(sketch, "E322.2", {"center": v(-2.5, 98.75) * mm, "radius": 1.55 * mm});
            skCircle(sketch, "E323.0", {"center": v(107.8, 92.3) * mm, "radius": 1.55 * mm});
            skCircle(sketch, "E323.1", {"center": v(114.25, 15) * mm, "radius": 1.55 * mm});
            skCircle(sketch, "E323.2", {"center": v(107.8, -62.3) * mm, "radius": 1.55 * mm});
            skCircle(sketch, "E323.3", {"center": v(-2.5, -68.75) * mm, "radius": 1.55 * mm});
            skCircle(sketch, "E324.0", {"center": v(-112.8, -62.3) * mm, "radius": 1.55 * mm});
            skCircle(sketch, "E325.0", {"center": v(-52.51, -47.97) * mm, "radius": 0.25 * mm});
            skCircle(sketch, "E326.0", {"center": v(47.51, -47.97) * mm, "radius": 0.25 * mm});
            skCircle(sketch, "E327.0", {"center": v(47.51, 77.97) * mm, "radius": 0.25 * mm});
            skCircle(sketch, "E327.1", {"center": v(-52.51, 77.97) * mm, "radius": 0.25 * mm});
            skSolve(sketch);
        }
        {
            var Q0;
            Q0=qSketchRegion(id+"F11",true);
            extrude(context, id + "F12", {"entities" : qUnion([Q0]), "depth" : (getVariable(context, 'PanelThickness')) * mm});
        }
        {
            var Q0;
            Q0=makeQuery(id+"F9.imprint","IMPRINT",FACE,{"disambiguationData":[TD([[makeQuery(id+"F9.imprint","IMPRINT",EDGE,{"derivedFrom":sQuery(id+"F9.wireOp",EDGE,"E302.0.0")}),1.0]])]});
            extrude(context, id + "F13", {"entities" : qUnion([Q0]), "oppositeDirection" : true, "depth" : (getVariable(context, 'PanelThickness')) * mm});
        }
        {
            var Q0;
            Q0=qCreatedBy(makeId("Top.planeOp"),FACE);
            var sketch = newSketch(context, id + "F14", { "sketchPlane" : qUnion([Q0])});
            skPoint(sketch, "E328.0", {"position": v(-201.64, -71.17) * mm});
            skPoint(sketch, "E328.1", {"position": v(-201.64, -141.17) * mm});
            skPoint(sketch, "E328.2", {"position": v(-21.64, -141.17) * mm});
            skPoint(sketch, "E328.3", {"position": v(-21.64, -71.17) * mm});
            skLineSegment(sketch, "E329.bottom", {"start": v(-201.64, -141.17) * mm, "end": v(-21.64, -141.17) * mm});
            skLineSegment(sketch, "E329.top", {"start": v(-201.64, -71.17) * mm, "end": v(-21.64, -71.17) * mm});
            skLineSegment(sketch, "E329.left", {"start": v(-201.64, -141.17) * mm, "end": v(-201.64, -71.17) * mm});
            skLineSegment(sketch, "E329.right", {"start": v(-21.64, -141.17) * mm, "end": v(-21.64, -71.17) * mm});
            skPoint(sketch, "E330.0", {"position": v(16.64, -141.17) * mm});
            skPoint(sketch, "E330.1", {"position": v(16.64, -71.17) * mm});
            skPoint(sketch, "E330.2", {"position": v(196.64, -71.17) * mm});
            skPoint(sketch, "E330.3", {"position": v(196.64, -141.17) * mm});
            skLineSegment(sketch, "E331.bottom", {"start": v(16.64, -141.17) * mm, "end": v(196.64, -141.17) * mm});
            skLineSegment(sketch, "E331.top", {"start": v(16.64, -71.17) * mm, "end": v(196.64, -71.17) * mm});
            skLineSegment(sketch, "E331.left", {"start": v(16.64, -141.17) * mm, "end": v(16.64, -71.17) * mm});
            skLineSegment(sketch, "E331.right", {"start": v(196.64, -141.17) * mm, "end": v(196.64, -71.17) * mm});
            skPoint(sketch, "E332", {"position": v(-201.64, -106.17) * mm});
            skPoint(sketch, "E333", {"position": v(-21.64, -106.17) * mm});
            skPoint(sketch, "E334", {"position": v(16.64, -106.17) * mm});
            skPoint(sketch, "E335", {"position": v(196.64, -106.17) * mm});
            skLineSegment(sketch, "E336", {"start": v(-201.64, -106.17) * mm, "end": v(-21.64, -106.17) * mm, "construction": true});
            skPoint(sketch, "E337", {"position": v(-156.64, -106.17) * mm});
            skPoint(sketch, "E338.1.0.0", {"position": v(-111.64, -106.17) * mm});
            skPoint(sketch, "E338.2.0.0", {"position": v(-66.64, -106.17) * mm});
            skLineSegment(sketch, "E338.direction1", {"start": v(-156.64, -106.17) * mm, "end": v(-111.64, -106.17) * mm, "construction": true});
            skLineSegment(sketch, "E339", {"start": v(-201.64, -106.17) * mm, "end": v(-156.64, -106.17) * mm, "construction": true});
            skLineSegment(sketch, "E340", {"start": v(-66.64, -106.17) * mm, "end": v(-21.64, -106.17) * mm, "construction": true});
            skCircle(sketch, "E341", {"center": v(-156.64, -106.17) * mm, "radius": 1.55 * mm});
            skCircle(sketch, "E342", {"center": v(-66.64, -106.17) * mm, "radius": 1.55 * mm});
            skLineSegment(sketch, "E343", {"start": v(-21.64, -106.17) * mm, "end": v(16.64, -106.17) * mm, "construction": true});
            skLineSegment(sketch, "E344", {"start": v(-2.5, -106.17) * mm, "end": v(-2.5, -72.72) * mm, "construction": true});
            skPoint(sketch, "E345", {"position": v(61.64, -106.17) * mm});
            skPoint(sketch, "E346", {"position": v(106.64, -106.17) * mm});
            skPoint(sketch, "E347", {"position": v(151.64, -106.17) * mm});
            skLineSegment(sketch, "E348", {"start": v(16.64, -106.17) * mm, "end": v(61.64, -106.17) * mm, "construction": true});
            skLineSegment(sketch, "E349", {"start": v(61.64, -106.17) * mm, "end": v(106.64, -106.17) * mm, "construction": true});
            skLineSegment(sketch, "E350", {"start": v(151.64, -106.17) * mm, "end": v(196.64, -106.17) * mm, "construction": true});
            skLineSegment(sketch, "E351", {"start": v(106.64, -106.17) * mm, "end": v(151.64, -106.17) * mm, "construction": true});
            skCircle(sketch, "E352", {"center": v(61.64, -106.17) * mm, "radius": 1.55 * mm});
            skCircle(sketch, "E353", {"center": v(151.64, -106.17) * mm, "radius": 1.55 * mm});
            skSolve(sketch);
        }
        {
            var Q0;
            Q0=qSketchRegion(id+"F14",true);
            extrude(context, id + "F15", {"entities" : qUnion([Q0]), "oppositeDirection" : true, "depth" : (getVariable(context, 'PanelThickness')) * mm});
        }
        {
            var Q0;
            Q0=qCreatedBy(makeId("Top.planeOp"),FACE);
            var sketch = newSketch(context, id + "F16", { "sketchPlane" : qUnion([Q0])});
            skLineSegment(sketch, "E354.0", {"start": v(-242, 130) * mm, "end": v(-242, -184) * mm});
            skLineSegment(sketch, "E354.2", {"start": v(-227, -199) * mm, "end": v(222, -199) * mm});
            skLineSegment(sketch, "E354.4", {"start": v(237, 140) * mm, "end": v(237, -184) * mm});
            skCircle(sketch, "E355.0", {"center": v(151.64, -106.17) * mm, "radius": 1.55 * mm});
            skCircle(sketch, "E356.0", {"center": v(61.64, -106.17) * mm, "radius": 1.55 * mm});
            skCircle(sketch, "E357.0", {"center": v(-66.64, -106.17) * mm, "radius": 1.55 * mm});
            skCircle(sketch, "E358.1", {"center": v(-156.64, -106.17) * mm, "radius": 1.55 * mm});
            skLineSegment(sketch, "E359.0", {"start": v(-201.64, -71.17) * mm, "end": v(-21.64, -71.17) * mm, "construction": true});
            skLineSegment(sketch, "E360", {"start": v(-242, -61.17) * mm, "end": v(237, -61.17) * mm});
            skArc(sketch, "E361.0", {"start": v(-242, -184) * mm, "mid": v(-237.6, -194.6) * mm, "end": v(-227, -199) * mm});
            skArc(sketch, "E362.1", {"start": v(222, -199) * mm, "mid": v(232.6, -194.6) * mm, "end": v(237, -184) * mm});
            skSolve(sketch);
        }
        {
            var Q0;
            Q0=qSketchRegion(id+"F16",true);
            extrude(context, id + "F17", {"entities" : qUnion([Q0]), "depth" : (getVariable(context, 'PanelThickness')) * mm});
        }
    });
